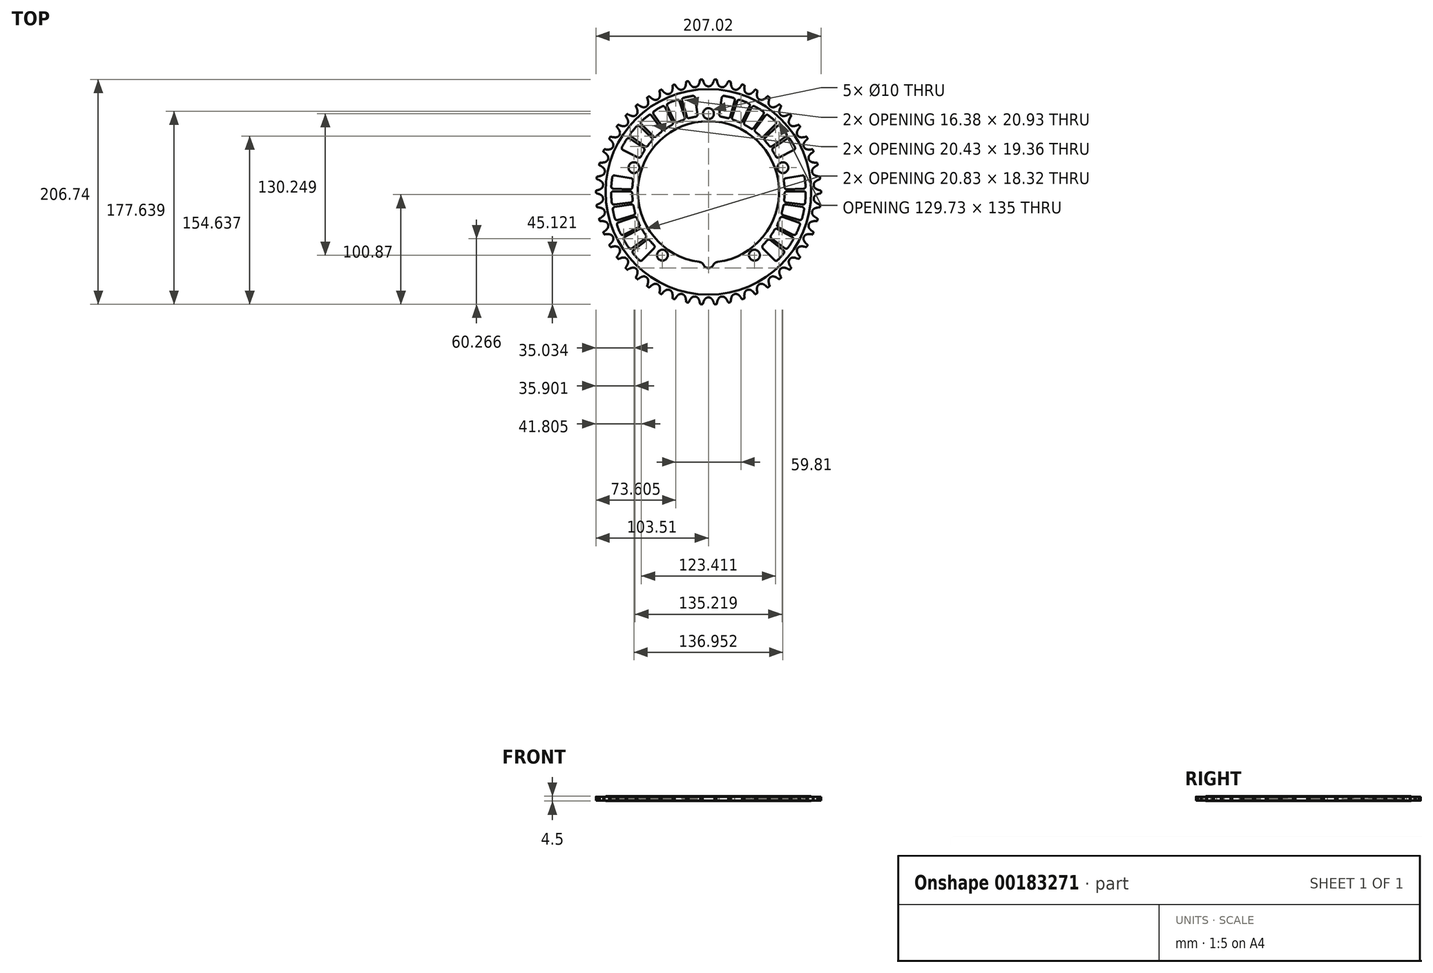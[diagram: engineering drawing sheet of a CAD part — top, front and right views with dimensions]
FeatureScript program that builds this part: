
annotation { "Feature Type Name" : "Feature", "Feature Type Description" : "" }
export const myFeature = defineFeature(function(context is Context, id is Id, definition is map)
    precondition{}
    {
        {
            var Q0;
            Q0=qCreatedBy(makeId("Top.planeOp"),FACE);
            var sketch = newSketch(context, id + "F0", { "sketchPlane" : qUnion([Q0])});
            skCircle(sketch, "E0", {"center": v(0, 0) * mm, "radius": 101.06 * mm, "construction": true});
            skCircle(sketch, "E1", {"center": v(0, 0) * mm, "radius": 65 * mm});
            skCircle(sketch, "E2", {"center": v(0, 72) * mm, "radius": 5 * mm});
            skCircle(sketch, "E3.1.0", {"center": v(-68.48, 22.25) * mm, "radius": 5 * mm});
            skCircle(sketch, "E3.2.0", {"center": v(-42.32, -58.25) * mm, "radius": 5 * mm});
            skCircle(sketch, "E3.3.0", {"center": v(42.32, -58.25) * mm, "radius": 5 * mm});
            skCircle(sketch, "E3.4.0", {"center": v(68.48, 22.25) * mm, "radius": 5 * mm});
            skCircle(sketch, "E4", {"center": v(0, 0) * mm, "radius": 94.55 * mm});
            skArc(sketch, "E5", {"start": v(-3.24, 98.7) * mm, "mid": v(-1.82, 97.48) * mm, "end": v(0, 97.05) * mm});
            skArc(sketch, "E6", {"start": v(-4.68, 101.38) * mm, "mid": v(-4.06, 99.98) * mm, "end": v(-3.24, 98.7) * mm});
            skLineSegment(sketch, "E7", {"start": v(-4.68, 101.38) * mm, "end": v(-5.06, 102.48) * mm});
            skArc(sketch, "E8.trimOffspring", {"start": v(-5.06, 102.48) * mm, "mid": v(-5.7, 103.79) * mm, "end": v(-6.6, 104.92) * mm});
            skArc(sketch, "E9.MirrorCS", {"start": v(3.24, 98.7) * mm, "mid": v(1.82, 97.48) * mm, "end": v(0, 97.05) * mm});
            skArc(sketch, "E10.MirrorCS", {"start": v(4.68, 101.38) * mm, "mid": v(4.06, 99.98) * mm, "end": v(3.24, 98.7) * mm});
            skLineSegment(sketch, "E11.MirrorCS", {"start": v(4.68, 101.38) * mm, "end": v(5.06, 102.48) * mm});
            skArc(sketch, "E12.MirrorCS", {"start": v(5.06, 102.48) * mm, "mid": v(5.7, 103.79) * mm, "end": v(6.6, 104.92) * mm});
            skArc(sketch, "E13.1.0", {"start": v(-17.87, 101.04) * mm, "mid": v(-18.66, 102.26) * mm, "end": v(-19.7, 103.26) * mm});
            skArc(sketch, "E13.1.1", {"start": v(-7.82, 102.31) * mm, "mid": v(-7.36, 103.68) * mm, "end": v(-6.6, 104.92) * mm});
            skLineSegment(sketch, "E13.1.2", {"start": v(-8.07, 101.17) * mm, "end": v(-7.82, 102.31) * mm});
            skArc(sketch, "E13.1.3", {"start": v(-8.07, 101.17) * mm, "mid": v(-8.5, 99.7) * mm, "end": v(-9.15, 98.32) * mm});
            skArc(sketch, "E13.1.4", {"start": v(-9.15, 98.32) * mm, "mid": v(-10.42, 96.94) * mm, "end": v(-12.16, 96.28) * mm});
            skArc(sketch, "E13.1.5", {"start": v(-15.58, 97.5) * mm, "mid": v(-14.02, 96.49) * mm, "end": v(-12.16, 96.28) * mm});
            skArc(sketch, "E13.1.6", {"start": v(-17.35, 100) * mm, "mid": v(-16.56, 98.69) * mm, "end": v(-15.58, 97.5) * mm});
            skLineSegment(sketch, "E13.1.7", {"start": v(-17.35, 100) * mm, "end": v(-17.87, 101.04) * mm});
            skArc(sketch, "E13.2.0", {"start": v(-30.39, 98) * mm, "mid": v(-31.33, 99.11) * mm, "end": v(-32.49, 99.98) * mm});
            skArc(sketch, "E13.2.1", {"start": v(-20.58, 100.52) * mm, "mid": v(-20.3, 101.94) * mm, "end": v(-19.7, 103.26) * mm});
            skLineSegment(sketch, "E13.2.2", {"start": v(-20.68, 99.36) * mm, "end": v(-20.58, 100.52) * mm});
            skArc(sketch, "E13.2.3", {"start": v(-20.68, 99.36) * mm, "mid": v(-20.94, 97.85) * mm, "end": v(-21.4, 96.4) * mm});
            skArc(sketch, "E13.2.4", {"start": v(-21.4, 96.4) * mm, "mid": v(-22.48, 94.87) * mm, "end": v(-24.13, 94) * mm});
            skArc(sketch, "E13.2.5", {"start": v(-27.68, 94.79) * mm, "mid": v(-26, 93.97) * mm, "end": v(-24.13, 94) * mm});
            skArc(sketch, "E13.2.6", {"start": v(-29.74, 97.03) * mm, "mid": v(-28.8, 95.83) * mm, "end": v(-27.68, 94.79) * mm});
            skLineSegment(sketch, "E13.2.7", {"start": v(-29.74, 97.03) * mm, "end": v(-30.39, 98) * mm});
            skArc(sketch, "E13.3.0", {"start": v(-42.43, 93.42) * mm, "mid": v(-43.5, 94.4) * mm, "end": v(-44.76, 95.12) * mm});
            skArc(sketch, "E13.3.1", {"start": v(-33.02, 97.15) * mm, "mid": v(-32.91, 98.6) * mm, "end": v(-32.49, 99.98) * mm});
            skLineSegment(sketch, "E13.3.2", {"start": v(-32.97, 95.98) * mm, "end": v(-33.02, 97.15) * mm});
            skArc(sketch, "E13.3.3", {"start": v(-32.97, 95.98) * mm, "mid": v(-33.03, 94.46) * mm, "end": v(-33.32, 92.95) * mm});
            skArc(sketch, "E13.3.4", {"start": v(-33.32, 92.95) * mm, "mid": v(-34.2, 91.3) * mm, "end": v(-35.73, 90.23) * mm});
            skArc(sketch, "E13.3.5", {"start": v(-39.34, 90.57) * mm, "mid": v(-37.57, 89.97) * mm, "end": v(-35.73, 90.23) * mm});
            skArc(sketch, "E13.3.6", {"start": v(-41.67, 92.54) * mm, "mid": v(-40.58, 91.47) * mm, "end": v(-39.34, 90.57) * mm});
            skLineSegment(sketch, "E13.3.7", {"start": v(-41.67, 92.54) * mm, "end": v(-42.43, 93.42) * mm});
            skArc(sketch, "E13.4.0", {"start": v(-53.8, 87.37) * mm, "mid": v(-54.99, 88.2) * mm, "end": v(-56.33, 88.76) * mm});
            skArc(sketch, "E13.4.1", {"start": v(-44.94, 92.25) * mm, "mid": v(-45.01, 93.7) * mm, "end": v(-44.76, 95.12) * mm});
            skLineSegment(sketch, "E13.4.2", {"start": v(-44.74, 91.1) * mm, "end": v(-44.94, 92.25) * mm});
            skArc(sketch, "E13.4.3", {"start": v(-44.74, 91.1) * mm, "mid": v(-44.61, 89.57) * mm, "end": v(-44.7, 88.05) * mm});
            skArc(sketch, "E13.4.4", {"start": v(-44.7, 88.05) * mm, "mid": v(-45.37, 86.3) * mm, "end": v(-46.75, 85.04) * mm});
            skArc(sketch, "E13.4.5", {"start": v(-50.38, 84.92) * mm, "mid": v(-48.55, 84.55) * mm, "end": v(-46.75, 85.04) * mm});
            skArc(sketch, "E13.4.6", {"start": v(-52.94, 86.59) * mm, "mid": v(-51.72, 85.66) * mm, "end": v(-50.38, 84.92) * mm});
            skLineSegment(sketch, "E13.4.7", {"start": v(-52.94, 86.59) * mm, "end": v(-53.8, 87.37) * mm});
            skArc(sketch, "E13.5.0", {"start": v(-64.33, 79.94) * mm, "mid": v(-65.61, 80.62) * mm, "end": v(-67, 81) * mm});
            skArc(sketch, "E13.5.1", {"start": v(-56.14, 85.89) * mm, "mid": v(-56.4, 87.31) * mm, "end": v(-56.33, 88.76) * mm});
            skLineSegment(sketch, "E13.5.2", {"start": v(-55.8, 84.77) * mm, "end": v(-56.14, 85.89) * mm});
            skArc(sketch, "E13.5.3", {"start": v(-55.8, 84.77) * mm, "mid": v(-55.49, 83.27) * mm, "end": v(-55.39, 81.75) * mm});
            skArc(sketch, "E13.5.4", {"start": v(-55.39, 81.75) * mm, "mid": v(-55.83, 79.93) * mm, "end": v(-57.04, 78.51) * mm});
            skArc(sketch, "E13.5.5", {"start": v(-60.63, 77.94) * mm, "mid": v(-58.77, 77.8) * mm, "end": v(-57.04, 78.51) * mm});
            skArc(sketch, "E13.5.6", {"start": v(-63.37, 79.27) * mm, "mid": v(-62.05, 78.5) * mm, "end": v(-60.63, 77.94) * mm});
            skLineSegment(sketch, "E13.5.7", {"start": v(-63.37, 79.27) * mm, "end": v(-64.33, 79.94) * mm});
            skArc(sketch, "E13.6.0", {"start": v(-73.85, 71.24) * mm, "mid": v(-75.2, 71.76) * mm, "end": v(-76.63, 71.96) * mm});
            skArc(sketch, "E13.6.1", {"start": v(-66.47, 78.17) * mm, "mid": v(-66.9, 79.56) * mm, "end": v(-67, 81) * mm});
            skLineSegment(sketch, "E13.6.2", {"start": v(-66, 77.1) * mm, "end": v(-66.47, 78.17) * mm});
            skArc(sketch, "E13.6.3", {"start": v(-66, 77.1) * mm, "mid": v(-65.49, 75.66) * mm, "end": v(-65.2, 74.16) * mm});
            skArc(sketch, "E13.6.4", {"start": v(-65.2, 74.16) * mm, "mid": v(-65.4, 72.3) * mm, "end": v(-66.43, 70.75) * mm});
            skArc(sketch, "E13.6.5", {"start": v(-69.92, 69.73) * mm, "mid": v(-68.06, 69.82) * mm, "end": v(-66.43, 70.75) * mm});
            skArc(sketch, "E13.6.6", {"start": v(-72.8, 70.7) * mm, "mid": v(-71.4, 70.1) * mm, "end": v(-69.92, 69.73) * mm});
            skLineSegment(sketch, "E13.6.7", {"start": v(-72.8, 70.7) * mm, "end": v(-73.85, 71.24) * mm});
            skArc(sketch, "E13.7.0", {"start": v(-82.2, 61.43) * mm, "mid": v(-83.6, 61.77) * mm, "end": v(-85.05, 61.8) * mm});
            skArc(sketch, "E13.7.1", {"start": v(-75.74, 69.23) * mm, "mid": v(-76.34, 70.54) * mm, "end": v(-76.63, 71.96) * mm});
            skLineSegment(sketch, "E13.7.2", {"start": v(-75.14, 68.23) * mm, "end": v(-75.74, 69.23) * mm});
            skArc(sketch, "E13.7.3", {"start": v(-75.14, 68.23) * mm, "mid": v(-74.45, 66.86) * mm, "end": v(-73.98, 65.4) * mm});
            skArc(sketch, "E13.7.4", {"start": v(-73.98, 65.4) * mm, "mid": v(-73.95, 63.54) * mm, "end": v(-74.78, 61.86) * mm});
            skArc(sketch, "E13.7.5", {"start": v(-78.1, 60.41) * mm, "mid": v(-76.27, 60.74) * mm, "end": v(-74.78, 61.86) * mm});
            skArc(sketch, "E13.7.6", {"start": v(-81.1, 61.02) * mm, "mid": v(-79.62, 60.6) * mm, "end": v(-78.1, 60.41) * mm});
            skLineSegment(sketch, "E13.7.7", {"start": v(-81.1, 61.02) * mm, "end": v(-82.2, 61.43) * mm});
            skArc(sketch, "E13.8.0", {"start": v(-89.24, 50.64) * mm, "mid": v(-90.68, 50.8) * mm, "end": v(-92.12, 50.64) * mm});
            skArc(sketch, "E13.8.1", {"start": v(-83.82, 59.19) * mm, "mid": v(-84.58, 60.42) * mm, "end": v(-85.05, 61.8) * mm});
            skLineSegment(sketch, "E13.8.2", {"start": v(-83.1, 58.27) * mm, "end": v(-83.82, 59.19) * mm});
            skArc(sketch, "E13.8.3", {"start": v(-83.1, 58.27) * mm, "mid": v(-82.25, 57) * mm, "end": v(-81.6, 55.62) * mm});
            skArc(sketch, "E13.8.4", {"start": v(-81.6, 55.62) * mm, "mid": v(-81.33, 53.77) * mm, "end": v(-81.94, 52) * mm});
            skArc(sketch, "E13.8.5", {"start": v(-85.06, 50.15) * mm, "mid": v(-83.28, 50.7) * mm, "end": v(-81.94, 52) * mm});
            skArc(sketch, "E13.8.6", {"start": v(-88.1, 50.38) * mm, "mid": v(-86.6, 50.15) * mm, "end": v(-85.06, 50.15) * mm});
            skLineSegment(sketch, "E13.8.7", {"start": v(-88.1, 50.38) * mm, "end": v(-89.24, 50.64) * mm});
            skArc(sketch, "E13.9.0", {"start": v(-94.89, 39.06) * mm, "mid": v(-96.33, 39.04) * mm, "end": v(-97.74, 38.7) * mm});
            skArc(sketch, "E13.9.1", {"start": v(-90.58, 48.22) * mm, "mid": v(-91.49, 49.34) * mm, "end": v(-92.12, 50.64) * mm});
            skLineSegment(sketch, "E13.9.2", {"start": v(-89.74, 47.4) * mm, "end": v(-90.58, 48.22) * mm});
            skArc(sketch, "E13.9.3", {"start": v(-89.74, 47.4) * mm, "mid": v(-88.74, 46.24) * mm, "end": v(-87.92, 44.95) * mm});
            skArc(sketch, "E13.9.4", {"start": v(-87.92, 44.95) * mm, "mid": v(-87.43, 43.15) * mm, "end": v(-87.81, 41.32) * mm});
            skArc(sketch, "E13.9.5", {"start": v(-90.68, 39.09) * mm, "mid": v(-88.98, 39.86) * mm, "end": v(-87.81, 41.32) * mm});
            skArc(sketch, "E13.9.6", {"start": v(-93.72, 38.94) * mm, "mid": v(-92.2, 38.9) * mm, "end": v(-90.68, 39.09) * mm});
            skLineSegment(sketch, "E13.9.7", {"start": v(-93.72, 38.94) * mm, "end": v(-94.89, 39.06) * mm});
            skArc(sketch, "E13.10.0", {"start": v(-99.03, 26.85) * mm, "mid": v(-100.47, 26.66) * mm, "end": v(-101.82, 26.14) * mm});
            skArc(sketch, "E13.10.1", {"start": v(-95.9, 36.48) * mm, "mid": v(-96.95, 37.49) * mm, "end": v(-97.74, 38.7) * mm});
            skLineSegment(sketch, "E13.10.2", {"start": v(-94.97, 35.78) * mm, "end": v(-95.9, 36.48) * mm});
            skArc(sketch, "E13.10.3", {"start": v(-94.97, 35.78) * mm, "mid": v(-93.84, 34.76) * mm, "end": v(-92.86, 33.58) * mm});
            skArc(sketch, "E13.10.4", {"start": v(-92.86, 33.58) * mm, "mid": v(-92.15, 31.85) * mm, "end": v(-92.3, 29.99) * mm});
            skArc(sketch, "E13.10.5", {"start": v(-94.86, 27.42) * mm, "mid": v(-93.27, 28.4) * mm, "end": v(-92.3, 29.99) * mm});
            skArc(sketch, "E13.10.6", {"start": v(-97.86, 26.88) * mm, "mid": v(-96.34, 27.04) * mm, "end": v(-94.86, 27.42) * mm});
            skLineSegment(sketch, "E13.10.7", {"start": v(-97.86, 26.88) * mm, "end": v(-99.03, 26.85) * mm});
            skArc(sketch, "E13.11.0", {"start": v(-101.62, 14.23) * mm, "mid": v(-103.02, 13.86) * mm, "end": v(-104.3, 13.18) * mm});
            skArc(sketch, "E13.11.1", {"start": v(-99.72, 24.18) * mm, "mid": v(-100.88, 25.04) * mm, "end": v(-101.82, 26.14) * mm});
            skLineSegment(sketch, "E13.11.2", {"start": v(-98.7, 23.59) * mm, "end": v(-99.72, 24.18) * mm});
            skArc(sketch, "E13.11.3", {"start": v(-98.7, 23.59) * mm, "mid": v(-97.45, 22.72) * mm, "end": v(-96.34, 21.68) * mm});
            skArc(sketch, "E13.11.4", {"start": v(-96.34, 21.68) * mm, "mid": v(-95.42, 20.05) * mm, "end": v(-95.33, 18.19) * mm});
            skArc(sketch, "E13.11.5", {"start": v(-97.55, 15.31) * mm, "mid": v(-96.1, 16.48) * mm, "end": v(-95.33, 18.19) * mm});
            skArc(sketch, "E13.11.6", {"start": v(-100.46, 14.4) * mm, "mid": v(-98.97, 14.75) * mm, "end": v(-97.55, 15.31) * mm});
            skLineSegment(sketch, "E13.11.7", {"start": v(-100.46, 14.4) * mm, "end": v(-101.62, 14.23) * mm});
            skArc(sketch, "E13.12.0", {"start": v(-102.6, 1.38) * mm, "mid": v(-103.94, 0.84) * mm, "end": v(-105.13, 0) * mm});
            skArc(sketch, "E13.12.1", {"start": v(-101.96, 11.49) * mm, "mid": v(-103.23, 12.2) * mm, "end": v(-104.3, 13.18) * mm});
            skLineSegment(sketch, "E13.12.2", {"start": v(-100.89, 11.03) * mm, "end": v(-101.96, 11.49) * mm});
            skArc(sketch, "E13.12.3", {"start": v(-100.89, 11.03) * mm, "mid": v(-99.53, 10.33) * mm, "end": v(-98.3, 9.43) * mm});
            skArc(sketch, "E13.12.4", {"start": v(-98.3, 9.43) * mm, "mid": v(-97.18, 7.93) * mm, "end": v(-96.86, 6.1) * mm});
            skArc(sketch, "E13.12.5", {"start": v(-98.7, 2.96) * mm, "mid": v(-97.4, 4.3) * mm, "end": v(-96.86, 6.1) * mm});
            skArc(sketch, "E13.12.6", {"start": v(-101.47, 1.7) * mm, "mid": v(-100.04, 2.23) * mm, "end": v(-98.7, 2.96) * mm});
            skLineSegment(sketch, "E13.12.7", {"start": v(-101.47, 1.7) * mm, "end": v(-102.6, 1.38) * mm});
            skArc(sketch, "E13.13.0", {"start": v(-101.96, -11.49) * mm, "mid": v(-103.23, -12.2) * mm, "end": v(-104.3, -13.18) * mm});
            skArc(sketch, "E13.13.1", {"start": v(-102.6, -1.38) * mm, "mid": v(-103.94, -0.84) * mm, "end": v(-105.13, 0) * mm});
            skLineSegment(sketch, "E13.13.2", {"start": v(-101.47, -1.7) * mm, "end": v(-102.6, -1.38) * mm});
            skArc(sketch, "E13.13.3", {"start": v(-101.47, -1.7) * mm, "mid": v(-100.04, -2.23) * mm, "end": v(-98.7, -2.96) * mm});
            skArc(sketch, "E13.13.4", {"start": v(-98.7, -2.96) * mm, "mid": v(-97.4, -4.3) * mm, "end": v(-96.86, -6.1) * mm});
            skArc(sketch, "E13.13.5", {"start": v(-98.3, -9.43) * mm, "mid": v(-97.18, -7.93) * mm, "end": v(-96.86, -6.1) * mm});
            skArc(sketch, "E13.13.6", {"start": v(-100.89, -11.03) * mm, "mid": v(-99.53, -10.33) * mm, "end": v(-98.3, -9.43) * mm});
            skLineSegment(sketch, "E13.13.7", {"start": v(-100.89, -11.03) * mm, "end": v(-101.96, -11.49) * mm});
            skArc(sketch, "E13.14.0", {"start": v(-99.72, -24.18) * mm, "mid": v(-100.88, -25.04) * mm, "end": v(-101.82, -26.14) * mm});
            skArc(sketch, "E13.14.1", {"start": v(-101.62, -14.23) * mm, "mid": v(-103.02, -13.86) * mm, "end": v(-104.3, -13.18) * mm});
            skLineSegment(sketch, "E13.14.2", {"start": v(-100.46, -14.4) * mm, "end": v(-101.62, -14.23) * mm});
            skArc(sketch, "E13.14.3", {"start": v(-100.46, -14.4) * mm, "mid": v(-98.97, -14.75) * mm, "end": v(-97.55, -15.31) * mm});
            skArc(sketch, "E13.14.4", {"start": v(-97.55, -15.31) * mm, "mid": v(-96.1, -16.48) * mm, "end": v(-95.33, -18.19) * mm});
            skArc(sketch, "E13.14.5", {"start": v(-96.34, -21.68) * mm, "mid": v(-95.42, -20.05) * mm, "end": v(-95.33, -18.19) * mm});
            skArc(sketch, "E13.14.6", {"start": v(-98.7, -23.59) * mm, "mid": v(-97.45, -22.72) * mm, "end": v(-96.34, -21.68) * mm});
            skLineSegment(sketch, "E13.14.7", {"start": v(-98.7, -23.59) * mm, "end": v(-99.72, -24.18) * mm});
            skArc(sketch, "E13.15.0", {"start": v(-95.9, -36.48) * mm, "mid": v(-96.95, -37.49) * mm, "end": v(-97.74, -38.7) * mm});
            skArc(sketch, "E13.15.1", {"start": v(-99.03, -26.85) * mm, "mid": v(-100.47, -26.66) * mm, "end": v(-101.82, -26.14) * mm});
            skLineSegment(sketch, "E13.15.2", {"start": v(-97.86, -26.88) * mm, "end": v(-99.03, -26.85) * mm});
            skArc(sketch, "E13.15.3", {"start": v(-97.86, -26.88) * mm, "mid": v(-96.34, -27.04) * mm, "end": v(-94.86, -27.42) * mm});
            skArc(sketch, "E13.15.4", {"start": v(-94.86, -27.42) * mm, "mid": v(-93.27, -28.4) * mm, "end": v(-92.3, -29.99) * mm});
            skArc(sketch, "E13.15.5", {"start": v(-92.86, -33.58) * mm, "mid": v(-92.15, -31.85) * mm, "end": v(-92.3, -29.99) * mm});
            skArc(sketch, "E13.15.6", {"start": v(-94.97, -35.78) * mm, "mid": v(-93.84, -34.76) * mm, "end": v(-92.86, -33.58) * mm});
            skLineSegment(sketch, "E13.15.7", {"start": v(-94.97, -35.78) * mm, "end": v(-95.9, -36.48) * mm});
            skArc(sketch, "E13.16.0", {"start": v(-90.58, -48.22) * mm, "mid": v(-91.49, -49.34) * mm, "end": v(-92.12, -50.64) * mm});
            skArc(sketch, "E13.16.1", {"start": v(-94.89, -39.06) * mm, "mid": v(-96.33, -39.04) * mm, "end": v(-97.74, -38.7) * mm});
            skLineSegment(sketch, "E13.16.2", {"start": v(-93.72, -38.94) * mm, "end": v(-94.89, -39.06) * mm});
            skArc(sketch, "E13.16.3", {"start": v(-93.72, -38.94) * mm, "mid": v(-92.2, -38.9) * mm, "end": v(-90.68, -39.09) * mm});
            skArc(sketch, "E13.16.4", {"start": v(-90.68, -39.09) * mm, "mid": v(-88.98, -39.86) * mm, "end": v(-87.81, -41.32) * mm});
            skArc(sketch, "E13.16.5", {"start": v(-87.92, -44.95) * mm, "mid": v(-87.43, -43.15) * mm, "end": v(-87.81, -41.32) * mm});
            skArc(sketch, "E13.16.6", {"start": v(-89.74, -47.4) * mm, "mid": v(-88.74, -46.24) * mm, "end": v(-87.92, -44.95) * mm});
            skLineSegment(sketch, "E13.16.7", {"start": v(-89.74, -47.4) * mm, "end": v(-90.58, -48.22) * mm});
            skArc(sketch, "E13.17.0", {"start": v(-83.82, -59.19) * mm, "mid": v(-84.58, -60.42) * mm, "end": v(-85.05, -61.8) * mm});
            skArc(sketch, "E13.17.1", {"start": v(-89.24, -50.64) * mm, "mid": v(-90.68, -50.8) * mm, "end": v(-92.12, -50.64) * mm});
            skLineSegment(sketch, "E13.17.2", {"start": v(-88.1, -50.38) * mm, "end": v(-89.24, -50.64) * mm});
            skArc(sketch, "E13.17.3", {"start": v(-88.1, -50.38) * mm, "mid": v(-86.6, -50.15) * mm, "end": v(-85.06, -50.15) * mm});
            skArc(sketch, "E13.17.4", {"start": v(-85.06, -50.15) * mm, "mid": v(-83.28, -50.7) * mm, "end": v(-81.94, -52) * mm});
            skArc(sketch, "E13.17.5", {"start": v(-81.6, -55.62) * mm, "mid": v(-81.33, -53.77) * mm, "end": v(-81.94, -52) * mm});
            skArc(sketch, "E13.17.6", {"start": v(-83.1, -58.27) * mm, "mid": v(-82.25, -57) * mm, "end": v(-81.6, -55.62) * mm});
            skLineSegment(sketch, "E13.17.7", {"start": v(-83.1, -58.27) * mm, "end": v(-83.82, -59.19) * mm});
            skArc(sketch, "E13.18.0", {"start": v(-75.74, -69.23) * mm, "mid": v(-76.34, -70.54) * mm, "end": v(-76.63, -71.96) * mm});
            skArc(sketch, "E13.18.1", {"start": v(-82.2, -61.43) * mm, "mid": v(-83.6, -61.77) * mm, "end": v(-85.05, -61.8) * mm});
            skLineSegment(sketch, "E13.18.2", {"start": v(-81.1, -61.02) * mm, "end": v(-82.2, -61.43) * mm});
            skArc(sketch, "E13.18.3", {"start": v(-81.1, -61.02) * mm, "mid": v(-79.62, -60.6) * mm, "end": v(-78.1, -60.41) * mm});
            skArc(sketch, "E13.18.4", {"start": v(-78.1, -60.41) * mm, "mid": v(-76.27, -60.74) * mm, "end": v(-74.78, -61.86) * mm});
            skArc(sketch, "E13.18.5", {"start": v(-73.98, -65.4) * mm, "mid": v(-73.95, -63.54) * mm, "end": v(-74.78, -61.86) * mm});
            skArc(sketch, "E13.18.6", {"start": v(-75.14, -68.23) * mm, "mid": v(-74.45, -66.86) * mm, "end": v(-73.98, -65.4) * mm});
            skLineSegment(sketch, "E13.18.7", {"start": v(-75.14, -68.23) * mm, "end": v(-75.74, -69.23) * mm});
            skArc(sketch, "E13.19.0", {"start": v(-66.47, -78.17) * mm, "mid": v(-66.9, -79.56) * mm, "end": v(-67, -81) * mm});
            skArc(sketch, "E13.19.1", {"start": v(-73.85, -71.24) * mm, "mid": v(-75.2, -71.76) * mm, "end": v(-76.63, -71.96) * mm});
            skLineSegment(sketch, "E13.19.2", {"start": v(-72.8, -70.7) * mm, "end": v(-73.85, -71.24) * mm});
            skArc(sketch, "E13.19.3", {"start": v(-72.8, -70.7) * mm, "mid": v(-71.4, -70.1) * mm, "end": v(-69.92, -69.73) * mm});
            skArc(sketch, "E13.19.4", {"start": v(-69.92, -69.73) * mm, "mid": v(-68.06, -69.82) * mm, "end": v(-66.43, -70.75) * mm});
            skArc(sketch, "E13.19.5", {"start": v(-65.2, -74.16) * mm, "mid": v(-65.4, -72.3) * mm, "end": v(-66.43, -70.75) * mm});
            skArc(sketch, "E13.19.6", {"start": v(-66, -77.1) * mm, "mid": v(-65.49, -75.66) * mm, "end": v(-65.2, -74.16) * mm});
            skLineSegment(sketch, "E13.19.7", {"start": v(-66, -77.1) * mm, "end": v(-66.47, -78.17) * mm});
            skArc(sketch, "E13.20.0", {"start": v(-56.14, -85.89) * mm, "mid": v(-56.4, -87.31) * mm, "end": v(-56.33, -88.76) * mm});
            skArc(sketch, "E13.20.1", {"start": v(-64.33, -79.94) * mm, "mid": v(-65.61, -80.62) * mm, "end": v(-67, -81) * mm});
            skLineSegment(sketch, "E13.20.2", {"start": v(-63.37, -79.27) * mm, "end": v(-64.33, -79.94) * mm});
            skArc(sketch, "E13.20.3", {"start": v(-63.37, -79.27) * mm, "mid": v(-62.05, -78.5) * mm, "end": v(-60.63, -77.94) * mm});
            skArc(sketch, "E13.20.4", {"start": v(-60.63, -77.94) * mm, "mid": v(-58.77, -77.8) * mm, "end": v(-57.04, -78.51) * mm});
            skArc(sketch, "E13.20.5", {"start": v(-55.39, -81.75) * mm, "mid": v(-55.83, -79.93) * mm, "end": v(-57.04, -78.51) * mm});
            skArc(sketch, "E13.20.6", {"start": v(-55.8, -84.77) * mm, "mid": v(-55.49, -83.27) * mm, "end": v(-55.39, -81.75) * mm});
            skLineSegment(sketch, "E13.20.7", {"start": v(-55.8, -84.77) * mm, "end": v(-56.14, -85.89) * mm});
            skArc(sketch, "E13.21.0", {"start": v(-44.94, -92.25) * mm, "mid": v(-45.01, -93.7) * mm, "end": v(-44.76, -95.12) * mm});
            skArc(sketch, "E13.21.1", {"start": v(-53.8, -87.37) * mm, "mid": v(-54.99, -88.2) * mm, "end": v(-56.33, -88.76) * mm});
            skLineSegment(sketch, "E13.21.2", {"start": v(-52.94, -86.59) * mm, "end": v(-53.8, -87.37) * mm});
            skArc(sketch, "E13.21.3", {"start": v(-52.94, -86.59) * mm, "mid": v(-51.72, -85.66) * mm, "end": v(-50.38, -84.92) * mm});
            skArc(sketch, "E13.21.4", {"start": v(-50.38, -84.92) * mm, "mid": v(-48.55, -84.55) * mm, "end": v(-46.75, -85.04) * mm});
            skArc(sketch, "E13.21.5", {"start": v(-44.7, -88.05) * mm, "mid": v(-45.37, -86.3) * mm, "end": v(-46.75, -85.04) * mm});
            skArc(sketch, "E13.21.6", {"start": v(-44.74, -91.1) * mm, "mid": v(-44.61, -89.57) * mm, "end": v(-44.7, -88.05) * mm});
            skLineSegment(sketch, "E13.21.7", {"start": v(-44.74, -91.1) * mm, "end": v(-44.94, -92.25) * mm});
            skArc(sketch, "E13.22.0", {"start": v(-33.02, -97.15) * mm, "mid": v(-32.91, -98.6) * mm, "end": v(-32.49, -99.98) * mm});
            skArc(sketch, "E13.22.1", {"start": v(-42.43, -93.42) * mm, "mid": v(-43.5, -94.4) * mm, "end": v(-44.76, -95.12) * mm});
            skLineSegment(sketch, "E13.22.2", {"start": v(-41.67, -92.54) * mm, "end": v(-42.43, -93.42) * mm});
            skArc(sketch, "E13.22.3", {"start": v(-41.67, -92.54) * mm, "mid": v(-40.58, -91.47) * mm, "end": v(-39.34, -90.57) * mm});
            skArc(sketch, "E13.22.4", {"start": v(-39.34, -90.57) * mm, "mid": v(-37.57, -89.97) * mm, "end": v(-35.73, -90.23) * mm});
            skArc(sketch, "E13.22.5", {"start": v(-33.32, -92.95) * mm, "mid": v(-34.2, -91.3) * mm, "end": v(-35.73, -90.23) * mm});
            skArc(sketch, "E13.22.6", {"start": v(-32.97, -95.98) * mm, "mid": v(-33.03, -94.46) * mm, "end": v(-33.32, -92.95) * mm});
            skLineSegment(sketch, "E13.22.7", {"start": v(-32.97, -95.98) * mm, "end": v(-33.02, -97.15) * mm});
            skArc(sketch, "E13.23.0", {"start": v(-20.58, -100.52) * mm, "mid": v(-20.3, -101.94) * mm, "end": v(-19.7, -103.26) * mm});
            skArc(sketch, "E13.23.1", {"start": v(-30.39, -98) * mm, "mid": v(-31.33, -99.11) * mm, "end": v(-32.49, -99.98) * mm});
            skLineSegment(sketch, "E13.23.2", {"start": v(-29.74, -97.03) * mm, "end": v(-30.39, -98) * mm});
            skArc(sketch, "E13.23.3", {"start": v(-29.74, -97.03) * mm, "mid": v(-28.8, -95.83) * mm, "end": v(-27.68, -94.79) * mm});
            skArc(sketch, "E13.23.4", {"start": v(-27.68, -94.79) * mm, "mid": v(-26, -93.97) * mm, "end": v(-24.13, -94) * mm});
            skArc(sketch, "E13.23.5", {"start": v(-21.4, -96.4) * mm, "mid": v(-22.48, -94.87) * mm, "end": v(-24.13, -94) * mm});
            skArc(sketch, "E13.23.6", {"start": v(-20.68, -99.36) * mm, "mid": v(-20.94, -97.85) * mm, "end": v(-21.4, -96.4) * mm});
            skLineSegment(sketch, "E13.23.7", {"start": v(-20.68, -99.36) * mm, "end": v(-20.58, -100.52) * mm});
            skArc(sketch, "E13.24.0", {"start": v(-7.82, -102.31) * mm, "mid": v(-7.36, -103.68) * mm, "end": v(-6.6, -104.92) * mm});
            skArc(sketch, "E13.24.1", {"start": v(-17.87, -101.04) * mm, "mid": v(-18.66, -102.26) * mm, "end": v(-19.7, -103.26) * mm});
            skLineSegment(sketch, "E13.24.2", {"start": v(-17.35, -100) * mm, "end": v(-17.87, -101.04) * mm});
            skArc(sketch, "E13.24.3", {"start": v(-17.35, -100) * mm, "mid": v(-16.56, -98.69) * mm, "end": v(-15.58, -97.5) * mm});
            skArc(sketch, "E13.24.4", {"start": v(-15.58, -97.5) * mm, "mid": v(-14.02, -96.49) * mm, "end": v(-12.16, -96.28) * mm});
            skArc(sketch, "E13.24.5", {"start": v(-9.15, -98.32) * mm, "mid": v(-10.42, -96.94) * mm, "end": v(-12.16, -96.28) * mm});
            skArc(sketch, "E13.24.6", {"start": v(-8.07, -101.17) * mm, "mid": v(-8.5, -99.7) * mm, "end": v(-9.15, -98.32) * mm});
            skLineSegment(sketch, "E13.24.7", {"start": v(-8.07, -101.17) * mm, "end": v(-7.82, -102.31) * mm});
            skArc(sketch, "E13.25.0", {"start": v(5.06, -102.48) * mm, "mid": v(5.7, -103.79) * mm, "end": v(6.6, -104.92) * mm});
            skArc(sketch, "E13.25.1", {"start": v(-5.06, -102.48) * mm, "mid": v(-5.7, -103.79) * mm, "end": v(-6.6, -104.92) * mm});
            skLineSegment(sketch, "E13.25.2", {"start": v(-4.68, -101.38) * mm, "end": v(-5.06, -102.48) * mm});
            skArc(sketch, "E13.25.3", {"start": v(-4.68, -101.38) * mm, "mid": v(-4.06, -99.98) * mm, "end": v(-3.24, -98.7) * mm});
            skArc(sketch, "E13.25.4", {"start": v(-3.24, -98.7) * mm, "mid": v(-1.82, -97.48) * mm, "end": v(0, -97.05) * mm});
            skArc(sketch, "E13.25.5", {"start": v(3.24, -98.7) * mm, "mid": v(1.82, -97.48) * mm, "end": v(0, -97.05) * mm});
            skArc(sketch, "E13.25.6", {"start": v(4.68, -101.38) * mm, "mid": v(4.06, -99.98) * mm, "end": v(3.24, -98.7) * mm});
            skLineSegment(sketch, "E13.25.7", {"start": v(4.68, -101.38) * mm, "end": v(5.06, -102.48) * mm});
            skArc(sketch, "E13.26.0", {"start": v(17.87, -101.04) * mm, "mid": v(18.66, -102.26) * mm, "end": v(19.7, -103.26) * mm});
            skArc(sketch, "E13.26.1", {"start": v(7.82, -102.31) * mm, "mid": v(7.36, -103.68) * mm, "end": v(6.6, -104.92) * mm});
            skLineSegment(sketch, "E13.26.2", {"start": v(8.07, -101.17) * mm, "end": v(7.82, -102.31) * mm});
            skArc(sketch, "E13.26.3", {"start": v(8.07, -101.17) * mm, "mid": v(8.5, -99.7) * mm, "end": v(9.15, -98.32) * mm});
            skArc(sketch, "E13.26.4", {"start": v(9.15, -98.32) * mm, "mid": v(10.42, -96.94) * mm, "end": v(12.16, -96.28) * mm});
            skArc(sketch, "E13.26.5", {"start": v(15.58, -97.5) * mm, "mid": v(14.02, -96.49) * mm, "end": v(12.16, -96.28) * mm});
            skArc(sketch, "E13.26.6", {"start": v(17.35, -100) * mm, "mid": v(16.56, -98.69) * mm, "end": v(15.58, -97.5) * mm});
            skLineSegment(sketch, "E13.26.7", {"start": v(17.35, -100) * mm, "end": v(17.87, -101.04) * mm});
            skArc(sketch, "E13.27.0", {"start": v(30.39, -98) * mm, "mid": v(31.33, -99.11) * mm, "end": v(32.49, -99.98) * mm});
            skArc(sketch, "E13.27.1", {"start": v(20.58, -100.52) * mm, "mid": v(20.3, -101.94) * mm, "end": v(19.7, -103.26) * mm});
            skLineSegment(sketch, "E13.27.2", {"start": v(20.68, -99.36) * mm, "end": v(20.58, -100.52) * mm});
            skArc(sketch, "E13.27.3", {"start": v(20.68, -99.36) * mm, "mid": v(20.94, -97.85) * mm, "end": v(21.4, -96.4) * mm});
            skArc(sketch, "E13.27.4", {"start": v(21.4, -96.4) * mm, "mid": v(22.48, -94.87) * mm, "end": v(24.13, -94) * mm});
            skArc(sketch, "E13.27.5", {"start": v(27.68, -94.79) * mm, "mid": v(26, -93.97) * mm, "end": v(24.13, -94) * mm});
            skArc(sketch, "E13.27.6", {"start": v(29.74, -97.03) * mm, "mid": v(28.8, -95.83) * mm, "end": v(27.68, -94.79) * mm});
            skLineSegment(sketch, "E13.27.7", {"start": v(29.74, -97.03) * mm, "end": v(30.39, -98) * mm});
            skArc(sketch, "E13.28.0", {"start": v(42.43, -93.42) * mm, "mid": v(43.5, -94.4) * mm, "end": v(44.76, -95.12) * mm});
            skArc(sketch, "E13.28.1", {"start": v(33.02, -97.15) * mm, "mid": v(32.91, -98.6) * mm, "end": v(32.49, -99.98) * mm});
            skLineSegment(sketch, "E13.28.2", {"start": v(32.97, -95.98) * mm, "end": v(33.02, -97.15) * mm});
            skArc(sketch, "E13.28.3", {"start": v(32.97, -95.98) * mm, "mid": v(33.03, -94.46) * mm, "end": v(33.32, -92.95) * mm});
            skArc(sketch, "E13.28.4", {"start": v(33.32, -92.95) * mm, "mid": v(34.2, -91.3) * mm, "end": v(35.73, -90.23) * mm});
            skArc(sketch, "E13.28.5", {"start": v(39.34, -90.57) * mm, "mid": v(37.57, -89.97) * mm, "end": v(35.73, -90.23) * mm});
            skArc(sketch, "E13.28.6", {"start": v(41.67, -92.54) * mm, "mid": v(40.58, -91.47) * mm, "end": v(39.34, -90.57) * mm});
            skLineSegment(sketch, "E13.28.7", {"start": v(41.67, -92.54) * mm, "end": v(42.43, -93.42) * mm});
            skArc(sketch, "E13.29.0", {"start": v(53.8, -87.37) * mm, "mid": v(54.99, -88.2) * mm, "end": v(56.33, -88.76) * mm});
            skArc(sketch, "E13.29.1", {"start": v(44.94, -92.25) * mm, "mid": v(45.01, -93.7) * mm, "end": v(44.76, -95.12) * mm});
            skLineSegment(sketch, "E13.29.2", {"start": v(44.74, -91.1) * mm, "end": v(44.94, -92.25) * mm});
            skArc(sketch, "E13.29.3", {"start": v(44.74, -91.1) * mm, "mid": v(44.61, -89.57) * mm, "end": v(44.7, -88.05) * mm});
            skArc(sketch, "E13.29.4", {"start": v(44.7, -88.05) * mm, "mid": v(45.37, -86.3) * mm, "end": v(46.75, -85.04) * mm});
            skArc(sketch, "E13.29.5", {"start": v(50.38, -84.92) * mm, "mid": v(48.55, -84.55) * mm, "end": v(46.75, -85.04) * mm});
            skArc(sketch, "E13.29.6", {"start": v(52.94, -86.59) * mm, "mid": v(51.72, -85.66) * mm, "end": v(50.38, -84.92) * mm});
            skLineSegment(sketch, "E13.29.7", {"start": v(52.94, -86.59) * mm, "end": v(53.8, -87.37) * mm});
            skArc(sketch, "E13.30.0", {"start": v(64.33, -79.94) * mm, "mid": v(65.61, -80.62) * mm, "end": v(67, -81) * mm});
            skArc(sketch, "E13.30.1", {"start": v(56.14, -85.89) * mm, "mid": v(56.4, -87.31) * mm, "end": v(56.33, -88.76) * mm});
            skLineSegment(sketch, "E13.30.2", {"start": v(55.8, -84.77) * mm, "end": v(56.14, -85.89) * mm});
            skArc(sketch, "E13.30.3", {"start": v(55.8, -84.77) * mm, "mid": v(55.49, -83.27) * mm, "end": v(55.39, -81.75) * mm});
            skArc(sketch, "E13.30.4", {"start": v(55.39, -81.75) * mm, "mid": v(55.83, -79.93) * mm, "end": v(57.04, -78.51) * mm});
            skArc(sketch, "E13.30.5", {"start": v(60.63, -77.94) * mm, "mid": v(58.77, -77.8) * mm, "end": v(57.04, -78.51) * mm});
            skArc(sketch, "E13.30.6", {"start": v(63.37, -79.27) * mm, "mid": v(62.05, -78.5) * mm, "end": v(60.63, -77.94) * mm});
            skLineSegment(sketch, "E13.30.7", {"start": v(63.37, -79.27) * mm, "end": v(64.33, -79.94) * mm});
            skArc(sketch, "E13.31.0", {"start": v(73.85, -71.24) * mm, "mid": v(75.2, -71.76) * mm, "end": v(76.63, -71.96) * mm});
            skArc(sketch, "E13.31.1", {"start": v(66.47, -78.17) * mm, "mid": v(66.9, -79.56) * mm, "end": v(67, -81) * mm});
            skLineSegment(sketch, "E13.31.2", {"start": v(66, -77.1) * mm, "end": v(66.47, -78.17) * mm});
            skArc(sketch, "E13.31.3", {"start": v(66, -77.1) * mm, "mid": v(65.49, -75.66) * mm, "end": v(65.2, -74.16) * mm});
            skArc(sketch, "E13.31.4", {"start": v(65.2, -74.16) * mm, "mid": v(65.4, -72.3) * mm, "end": v(66.43, -70.75) * mm});
            skArc(sketch, "E13.31.5", {"start": v(69.92, -69.73) * mm, "mid": v(68.06, -69.82) * mm, "end": v(66.43, -70.75) * mm});
            skArc(sketch, "E13.31.6", {"start": v(72.8, -70.7) * mm, "mid": v(71.4, -70.1) * mm, "end": v(69.92, -69.73) * mm});
            skLineSegment(sketch, "E13.31.7", {"start": v(72.8, -70.7) * mm, "end": v(73.85, -71.24) * mm});
            skArc(sketch, "E13.32.0", {"start": v(82.2, -61.43) * mm, "mid": v(83.6, -61.77) * mm, "end": v(85.05, -61.8) * mm});
            skArc(sketch, "E13.32.1", {"start": v(75.74, -69.23) * mm, "mid": v(76.34, -70.54) * mm, "end": v(76.63, -71.96) * mm});
            skLineSegment(sketch, "E13.32.2", {"start": v(75.14, -68.23) * mm, "end": v(75.74, -69.23) * mm});
            skArc(sketch, "E13.32.3", {"start": v(75.14, -68.23) * mm, "mid": v(74.45, -66.86) * mm, "end": v(73.98, -65.4) * mm});
            skArc(sketch, "E13.32.4", {"start": v(73.98, -65.4) * mm, "mid": v(73.95, -63.54) * mm, "end": v(74.78, -61.86) * mm});
            skArc(sketch, "E13.32.5", {"start": v(78.1, -60.41) * mm, "mid": v(76.27, -60.74) * mm, "end": v(74.78, -61.86) * mm});
            skArc(sketch, "E13.32.6", {"start": v(81.1, -61.02) * mm, "mid": v(79.62, -60.6) * mm, "end": v(78.1, -60.41) * mm});
            skLineSegment(sketch, "E13.32.7", {"start": v(81.1, -61.02) * mm, "end": v(82.2, -61.43) * mm});
            skArc(sketch, "E13.33.0", {"start": v(89.24, -50.64) * mm, "mid": v(90.68, -50.8) * mm, "end": v(92.12, -50.64) * mm});
            skArc(sketch, "E13.33.1", {"start": v(83.82, -59.19) * mm, "mid": v(84.58, -60.42) * mm, "end": v(85.05, -61.8) * mm});
            skLineSegment(sketch, "E13.33.2", {"start": v(83.1, -58.27) * mm, "end": v(83.82, -59.19) * mm});
            skArc(sketch, "E13.33.3", {"start": v(83.1, -58.27) * mm, "mid": v(82.25, -57) * mm, "end": v(81.6, -55.62) * mm});
            skArc(sketch, "E13.33.4", {"start": v(81.6, -55.62) * mm, "mid": v(81.33, -53.77) * mm, "end": v(81.94, -52) * mm});
            skArc(sketch, "E13.33.5", {"start": v(85.06, -50.15) * mm, "mid": v(83.28, -50.7) * mm, "end": v(81.94, -52) * mm});
            skArc(sketch, "E13.33.6", {"start": v(88.1, -50.38) * mm, "mid": v(86.6, -50.15) * mm, "end": v(85.06, -50.15) * mm});
            skLineSegment(sketch, "E13.33.7", {"start": v(88.1, -50.38) * mm, "end": v(89.24, -50.64) * mm});
            skArc(sketch, "E13.34.0", {"start": v(94.89, -39.06) * mm, "mid": v(96.33, -39.04) * mm, "end": v(97.74, -38.7) * mm});
            skArc(sketch, "E13.34.1", {"start": v(90.58, -48.22) * mm, "mid": v(91.49, -49.34) * mm, "end": v(92.12, -50.64) * mm});
            skLineSegment(sketch, "E13.34.2", {"start": v(89.74, -47.4) * mm, "end": v(90.58, -48.22) * mm});
            skArc(sketch, "E13.34.3", {"start": v(89.74, -47.4) * mm, "mid": v(88.74, -46.24) * mm, "end": v(87.92, -44.95) * mm});
            skArc(sketch, "E13.34.4", {"start": v(87.92, -44.95) * mm, "mid": v(87.43, -43.15) * mm, "end": v(87.81, -41.32) * mm});
            skArc(sketch, "E13.34.5", {"start": v(90.68, -39.09) * mm, "mid": v(88.98, -39.86) * mm, "end": v(87.81, -41.32) * mm});
            skArc(sketch, "E13.34.6", {"start": v(93.72, -38.94) * mm, "mid": v(92.2, -38.9) * mm, "end": v(90.68, -39.09) * mm});
            skLineSegment(sketch, "E13.34.7", {"start": v(93.72, -38.94) * mm, "end": v(94.89, -39.06) * mm});
            skArc(sketch, "E13.35.0", {"start": v(99.03, -26.85) * mm, "mid": v(100.47, -26.66) * mm, "end": v(101.82, -26.14) * mm});
            skArc(sketch, "E13.35.1", {"start": v(95.9, -36.48) * mm, "mid": v(96.95, -37.49) * mm, "end": v(97.74, -38.7) * mm});
            skLineSegment(sketch, "E13.35.2", {"start": v(94.97, -35.78) * mm, "end": v(95.9, -36.48) * mm});
            skArc(sketch, "E13.35.3", {"start": v(94.97, -35.78) * mm, "mid": v(93.84, -34.76) * mm, "end": v(92.86, -33.58) * mm});
            skArc(sketch, "E13.35.4", {"start": v(92.86, -33.58) * mm, "mid": v(92.15, -31.85) * mm, "end": v(92.3, -29.99) * mm});
            skArc(sketch, "E13.35.5", {"start": v(94.86, -27.42) * mm, "mid": v(93.27, -28.4) * mm, "end": v(92.3, -29.99) * mm});
            skArc(sketch, "E13.35.6", {"start": v(97.86, -26.88) * mm, "mid": v(96.34, -27.04) * mm, "end": v(94.86, -27.42) * mm});
            skLineSegment(sketch, "E13.35.7", {"start": v(97.86, -26.88) * mm, "end": v(99.03, -26.85) * mm});
            skArc(sketch, "E13.36.0", {"start": v(101.62, -14.23) * mm, "mid": v(103.02, -13.86) * mm, "end": v(104.3, -13.18) * mm});
            skArc(sketch, "E13.36.1", {"start": v(99.72, -24.18) * mm, "mid": v(100.88, -25.04) * mm, "end": v(101.82, -26.14) * mm});
            skLineSegment(sketch, "E13.36.2", {"start": v(98.7, -23.59) * mm, "end": v(99.72, -24.18) * mm});
            skArc(sketch, "E13.36.3", {"start": v(98.7, -23.59) * mm, "mid": v(97.45, -22.72) * mm, "end": v(96.34, -21.68) * mm});
            skArc(sketch, "E13.36.4", {"start": v(96.34, -21.68) * mm, "mid": v(95.42, -20.05) * mm, "end": v(95.33, -18.19) * mm});
            skArc(sketch, "E13.36.5", {"start": v(97.55, -15.31) * mm, "mid": v(96.1, -16.48) * mm, "end": v(95.33, -18.19) * mm});
            skArc(sketch, "E13.36.6", {"start": v(100.46, -14.4) * mm, "mid": v(98.97, -14.75) * mm, "end": v(97.55, -15.31) * mm});
            skLineSegment(sketch, "E13.36.7", {"start": v(100.46, -14.4) * mm, "end": v(101.62, -14.23) * mm});
            skArc(sketch, "E13.37.0", {"start": v(102.6, -1.38) * mm, "mid": v(103.94, -0.84) * mm, "end": v(105.13, 0) * mm});
            skArc(sketch, "E13.37.1", {"start": v(101.96, -11.49) * mm, "mid": v(103.23, -12.2) * mm, "end": v(104.3, -13.18) * mm});
            skLineSegment(sketch, "E13.37.2", {"start": v(100.89, -11.03) * mm, "end": v(101.96, -11.49) * mm});
            skArc(sketch, "E13.37.3", {"start": v(100.89, -11.03) * mm, "mid": v(99.53, -10.33) * mm, "end": v(98.3, -9.43) * mm});
            skArc(sketch, "E13.37.4", {"start": v(98.3, -9.43) * mm, "mid": v(97.18, -7.93) * mm, "end": v(96.86, -6.1) * mm});
            skArc(sketch, "E13.37.5", {"start": v(98.7, -2.96) * mm, "mid": v(97.4, -4.3) * mm, "end": v(96.86, -6.1) * mm});
            skArc(sketch, "E13.37.6", {"start": v(101.47, -1.7) * mm, "mid": v(100.04, -2.23) * mm, "end": v(98.7, -2.96) * mm});
            skLineSegment(sketch, "E13.37.7", {"start": v(101.47, -1.7) * mm, "end": v(102.6, -1.38) * mm});
            skArc(sketch, "E13.38.0", {"start": v(101.96, 11.49) * mm, "mid": v(103.23, 12.2) * mm, "end": v(104.3, 13.18) * mm});
            skArc(sketch, "E13.38.1", {"start": v(102.6, 1.38) * mm, "mid": v(103.94, 0.84) * mm, "end": v(105.13, 0) * mm});
            skLineSegment(sketch, "E13.38.2", {"start": v(101.47, 1.7) * mm, "end": v(102.6, 1.38) * mm});
            skArc(sketch, "E13.38.3", {"start": v(101.47, 1.7) * mm, "mid": v(100.04, 2.23) * mm, "end": v(98.7, 2.96) * mm});
            skArc(sketch, "E13.38.4", {"start": v(98.7, 2.96) * mm, "mid": v(97.4, 4.3) * mm, "end": v(96.86, 6.1) * mm});
            skArc(sketch, "E13.38.5", {"start": v(98.3, 9.43) * mm, "mid": v(97.18, 7.93) * mm, "end": v(96.86, 6.1) * mm});
            skArc(sketch, "E13.38.6", {"start": v(100.89, 11.03) * mm, "mid": v(99.53, 10.33) * mm, "end": v(98.3, 9.43) * mm});
            skLineSegment(sketch, "E13.38.7", {"start": v(100.89, 11.03) * mm, "end": v(101.96, 11.49) * mm});
            skArc(sketch, "E13.39.0", {"start": v(99.72, 24.18) * mm, "mid": v(100.88, 25.04) * mm, "end": v(101.82, 26.14) * mm});
            skArc(sketch, "E13.39.1", {"start": v(101.62, 14.23) * mm, "mid": v(103.02, 13.86) * mm, "end": v(104.3, 13.18) * mm});
            skLineSegment(sketch, "E13.39.2", {"start": v(100.46, 14.4) * mm, "end": v(101.62, 14.23) * mm});
            skArc(sketch, "E13.39.3", {"start": v(100.46, 14.4) * mm, "mid": v(98.97, 14.75) * mm, "end": v(97.55, 15.31) * mm});
            skArc(sketch, "E13.39.4", {"start": v(97.55, 15.31) * mm, "mid": v(96.1, 16.48) * mm, "end": v(95.33, 18.19) * mm});
            skArc(sketch, "E13.39.5", {"start": v(96.34, 21.68) * mm, "mid": v(95.42, 20.05) * mm, "end": v(95.33, 18.19) * mm});
            skArc(sketch, "E13.39.6", {"start": v(98.7, 23.59) * mm, "mid": v(97.45, 22.72) * mm, "end": v(96.34, 21.68) * mm});
            skLineSegment(sketch, "E13.39.7", {"start": v(98.7, 23.59) * mm, "end": v(99.72, 24.18) * mm});
            skArc(sketch, "E13.40.0", {"start": v(95.9, 36.48) * mm, "mid": v(96.95, 37.49) * mm, "end": v(97.74, 38.7) * mm});
            skArc(sketch, "E13.40.1", {"start": v(99.03, 26.85) * mm, "mid": v(100.47, 26.66) * mm, "end": v(101.82, 26.14) * mm});
            skLineSegment(sketch, "E13.40.2", {"start": v(97.86, 26.88) * mm, "end": v(99.03, 26.85) * mm});
            skArc(sketch, "E13.40.3", {"start": v(97.86, 26.88) * mm, "mid": v(96.34, 27.04) * mm, "end": v(94.86, 27.42) * mm});
            skArc(sketch, "E13.40.4", {"start": v(94.86, 27.42) * mm, "mid": v(93.27, 28.4) * mm, "end": v(92.3, 29.99) * mm});
            skArc(sketch, "E13.40.5", {"start": v(92.86, 33.58) * mm, "mid": v(92.15, 31.85) * mm, "end": v(92.3, 29.99) * mm});
            skArc(sketch, "E13.40.6", {"start": v(94.97, 35.78) * mm, "mid": v(93.84, 34.76) * mm, "end": v(92.86, 33.58) * mm});
            skLineSegment(sketch, "E13.40.7", {"start": v(94.97, 35.78) * mm, "end": v(95.9, 36.48) * mm});
            skArc(sketch, "E13.41.0", {"start": v(90.58, 48.22) * mm, "mid": v(91.49, 49.34) * mm, "end": v(92.12, 50.64) * mm});
            skArc(sketch, "E13.41.1", {"start": v(94.89, 39.06) * mm, "mid": v(96.33, 39.04) * mm, "end": v(97.74, 38.7) * mm});
            skLineSegment(sketch, "E13.41.2", {"start": v(93.72, 38.94) * mm, "end": v(94.89, 39.06) * mm});
            skArc(sketch, "E13.41.3", {"start": v(93.72, 38.94) * mm, "mid": v(92.2, 38.9) * mm, "end": v(90.68, 39.09) * mm});
            skArc(sketch, "E13.41.4", {"start": v(90.68, 39.09) * mm, "mid": v(88.98, 39.86) * mm, "end": v(87.81, 41.32) * mm});
            skArc(sketch, "E13.41.5", {"start": v(87.92, 44.95) * mm, "mid": v(87.43, 43.15) * mm, "end": v(87.81, 41.32) * mm});
            skArc(sketch, "E13.41.6", {"start": v(89.74, 47.4) * mm, "mid": v(88.74, 46.24) * mm, "end": v(87.92, 44.95) * mm});
            skLineSegment(sketch, "E13.41.7", {"start": v(89.74, 47.4) * mm, "end": v(90.58, 48.22) * mm});
            skArc(sketch, "E13.42.0", {"start": v(83.82, 59.19) * mm, "mid": v(84.58, 60.42) * mm, "end": v(85.05, 61.8) * mm});
            skArc(sketch, "E13.42.1", {"start": v(89.24, 50.64) * mm, "mid": v(90.68, 50.8) * mm, "end": v(92.12, 50.64) * mm});
            skLineSegment(sketch, "E13.42.2", {"start": v(88.1, 50.38) * mm, "end": v(89.24, 50.64) * mm});
            skArc(sketch, "E13.42.3", {"start": v(88.1, 50.38) * mm, "mid": v(86.6, 50.15) * mm, "end": v(85.06, 50.15) * mm});
            skArc(sketch, "E13.42.4", {"start": v(85.06, 50.15) * mm, "mid": v(83.28, 50.7) * mm, "end": v(81.94, 52) * mm});
            skArc(sketch, "E13.42.5", {"start": v(81.6, 55.62) * mm, "mid": v(81.33, 53.77) * mm, "end": v(81.94, 52) * mm});
            skArc(sketch, "E13.42.6", {"start": v(83.1, 58.27) * mm, "mid": v(82.25, 57) * mm, "end": v(81.6, 55.62) * mm});
            skLineSegment(sketch, "E13.42.7", {"start": v(83.1, 58.27) * mm, "end": v(83.82, 59.19) * mm});
            skArc(sketch, "E13.43.0", {"start": v(75.74, 69.23) * mm, "mid": v(76.34, 70.54) * mm, "end": v(76.63, 71.96) * mm});
            skArc(sketch, "E13.43.1", {"start": v(82.2, 61.43) * mm, "mid": v(83.6, 61.77) * mm, "end": v(85.05, 61.8) * mm});
            skLineSegment(sketch, "E13.43.2", {"start": v(81.1, 61.02) * mm, "end": v(82.2, 61.43) * mm});
            skArc(sketch, "E13.43.3", {"start": v(81.1, 61.02) * mm, "mid": v(79.62, 60.6) * mm, "end": v(78.1, 60.41) * mm});
            skArc(sketch, "E13.43.4", {"start": v(78.1, 60.41) * mm, "mid": v(76.27, 60.74) * mm, "end": v(74.78, 61.86) * mm});
            skArc(sketch, "E13.43.5", {"start": v(73.98, 65.4) * mm, "mid": v(73.95, 63.54) * mm, "end": v(74.78, 61.86) * mm});
            skArc(sketch, "E13.43.6", {"start": v(75.14, 68.23) * mm, "mid": v(74.45, 66.86) * mm, "end": v(73.98, 65.4) * mm});
            skLineSegment(sketch, "E13.43.7", {"start": v(75.14, 68.23) * mm, "end": v(75.74, 69.23) * mm});
            skArc(sketch, "E13.44.0", {"start": v(66.47, 78.17) * mm, "mid": v(66.9, 79.56) * mm, "end": v(67, 81) * mm});
            skArc(sketch, "E13.44.1", {"start": v(73.85, 71.24) * mm, "mid": v(75.2, 71.76) * mm, "end": v(76.63, 71.96) * mm});
            skLineSegment(sketch, "E13.44.2", {"start": v(72.8, 70.7) * mm, "end": v(73.85, 71.24) * mm});
            skArc(sketch, "E13.44.3", {"start": v(72.8, 70.7) * mm, "mid": v(71.4, 70.1) * mm, "end": v(69.92, 69.73) * mm});
            skArc(sketch, "E13.44.4", {"start": v(69.92, 69.73) * mm, "mid": v(68.06, 69.82) * mm, "end": v(66.43, 70.75) * mm});
            skArc(sketch, "E13.44.5", {"start": v(65.2, 74.16) * mm, "mid": v(65.4, 72.3) * mm, "end": v(66.43, 70.75) * mm});
            skArc(sketch, "E13.44.6", {"start": v(66, 77.1) * mm, "mid": v(65.49, 75.66) * mm, "end": v(65.2, 74.16) * mm});
            skLineSegment(sketch, "E13.44.7", {"start": v(66, 77.1) * mm, "end": v(66.47, 78.17) * mm});
            skArc(sketch, "E13.45.0", {"start": v(56.14, 85.89) * mm, "mid": v(56.4, 87.31) * mm, "end": v(56.33, 88.76) * mm});
            skArc(sketch, "E13.45.1", {"start": v(64.33, 79.94) * mm, "mid": v(65.61, 80.62) * mm, "end": v(67, 81) * mm});
            skLineSegment(sketch, "E13.45.2", {"start": v(63.37, 79.27) * mm, "end": v(64.33, 79.94) * mm});
            skArc(sketch, "E13.45.3", {"start": v(63.37, 79.27) * mm, "mid": v(62.05, 78.5) * mm, "end": v(60.63, 77.94) * mm});
            skArc(sketch, "E13.45.4", {"start": v(60.63, 77.94) * mm, "mid": v(58.77, 77.8) * mm, "end": v(57.04, 78.51) * mm});
            skArc(sketch, "E13.45.5", {"start": v(55.39, 81.75) * mm, "mid": v(55.83, 79.93) * mm, "end": v(57.04, 78.51) * mm});
            skArc(sketch, "E13.45.6", {"start": v(55.8, 84.77) * mm, "mid": v(55.49, 83.27) * mm, "end": v(55.39, 81.75) * mm});
            skLineSegment(sketch, "E13.45.7", {"start": v(55.8, 84.77) * mm, "end": v(56.14, 85.89) * mm});
            skArc(sketch, "E13.46.0", {"start": v(44.94, 92.25) * mm, "mid": v(45.01, 93.7) * mm, "end": v(44.76, 95.12) * mm});
            skArc(sketch, "E13.46.1", {"start": v(53.8, 87.37) * mm, "mid": v(54.99, 88.2) * mm, "end": v(56.33, 88.76) * mm});
            skLineSegment(sketch, "E13.46.2", {"start": v(52.94, 86.59) * mm, "end": v(53.8, 87.37) * mm});
            skArc(sketch, "E13.46.3", {"start": v(52.94, 86.59) * mm, "mid": v(51.72, 85.66) * mm, "end": v(50.38, 84.92) * mm});
            skArc(sketch, "E13.46.4", {"start": v(50.38, 84.92) * mm, "mid": v(48.55, 84.55) * mm, "end": v(46.75, 85.04) * mm});
            skArc(sketch, "E13.46.5", {"start": v(44.7, 88.05) * mm, "mid": v(45.37, 86.3) * mm, "end": v(46.75, 85.04) * mm});
            skArc(sketch, "E13.46.6", {"start": v(44.74, 91.1) * mm, "mid": v(44.61, 89.57) * mm, "end": v(44.7, 88.05) * mm});
            skLineSegment(sketch, "E13.46.7", {"start": v(44.74, 91.1) * mm, "end": v(44.94, 92.25) * mm});
            skArc(sketch, "E13.47.0", {"start": v(33.02, 97.15) * mm, "mid": v(32.91, 98.6) * mm, "end": v(32.49, 99.98) * mm});
            skArc(sketch, "E13.47.1", {"start": v(42.43, 93.42) * mm, "mid": v(43.5, 94.4) * mm, "end": v(44.76, 95.12) * mm});
            skLineSegment(sketch, "E13.47.2", {"start": v(41.67, 92.54) * mm, "end": v(42.43, 93.42) * mm});
            skArc(sketch, "E13.47.3", {"start": v(41.67, 92.54) * mm, "mid": v(40.58, 91.47) * mm, "end": v(39.34, 90.57) * mm});
            skArc(sketch, "E13.47.4", {"start": v(39.34, 90.57) * mm, "mid": v(37.57, 89.97) * mm, "end": v(35.73, 90.23) * mm});
            skArc(sketch, "E13.47.5", {"start": v(33.32, 92.95) * mm, "mid": v(34.2, 91.3) * mm, "end": v(35.73, 90.23) * mm});
            skArc(sketch, "E13.47.6", {"start": v(32.97, 95.98) * mm, "mid": v(33.03, 94.46) * mm, "end": v(33.32, 92.95) * mm});
            skLineSegment(sketch, "E13.47.7", {"start": v(32.97, 95.98) * mm, "end": v(33.02, 97.15) * mm});
            skArc(sketch, "E13.48.0", {"start": v(20.58, 100.52) * mm, "mid": v(20.3, 101.94) * mm, "end": v(19.7, 103.26) * mm});
            skArc(sketch, "E13.48.1", {"start": v(30.39, 98) * mm, "mid": v(31.33, 99.11) * mm, "end": v(32.49, 99.98) * mm});
            skLineSegment(sketch, "E13.48.2", {"start": v(29.74, 97.03) * mm, "end": v(30.39, 98) * mm});
            skArc(sketch, "E13.48.3", {"start": v(29.74, 97.03) * mm, "mid": v(28.8, 95.83) * mm, "end": v(27.68, 94.79) * mm});
            skArc(sketch, "E13.48.4", {"start": v(27.68, 94.79) * mm, "mid": v(26, 93.97) * mm, "end": v(24.13, 94) * mm});
            skArc(sketch, "E13.48.5", {"start": v(21.4, 96.4) * mm, "mid": v(22.48, 94.87) * mm, "end": v(24.13, 94) * mm});
            skArc(sketch, "E13.48.6", {"start": v(20.68, 99.36) * mm, "mid": v(20.94, 97.85) * mm, "end": v(21.4, 96.4) * mm});
            skLineSegment(sketch, "E13.48.7", {"start": v(20.68, 99.36) * mm, "end": v(20.58, 100.52) * mm});
            skArc(sketch, "E13.49.0", {"start": v(7.82, 102.31) * mm, "mid": v(7.36, 103.68) * mm, "end": v(6.6, 104.92) * mm});
            skArc(sketch, "E13.49.1", {"start": v(17.87, 101.04) * mm, "mid": v(18.66, 102.26) * mm, "end": v(19.7, 103.26) * mm});
            skLineSegment(sketch, "E13.49.2", {"start": v(17.35, 100) * mm, "end": v(17.87, 101.04) * mm});
            skArc(sketch, "E13.49.3", {"start": v(17.35, 100) * mm, "mid": v(16.56, 98.69) * mm, "end": v(15.58, 97.5) * mm});
            skArc(sketch, "E13.49.4", {"start": v(15.58, 97.5) * mm, "mid": v(14.02, 96.49) * mm, "end": v(12.16, 96.28) * mm});
            skArc(sketch, "E13.49.5", {"start": v(9.15, 98.32) * mm, "mid": v(10.42, 96.94) * mm, "end": v(12.16, 96.28) * mm});
            skArc(sketch, "E13.49.6", {"start": v(8.07, 101.17) * mm, "mid": v(8.5, 99.7) * mm, "end": v(9.15, 98.32) * mm});
            skLineSegment(sketch, "E13.49.7", {"start": v(8.07, 101.17) * mm, "end": v(7.82, 102.31) * mm});
            skCircle(sketch, "E14", {"center": v(0, 0) * mm, "radius": 103.5 * mm});
            skCircle(sketch, "E15", {"center": v(0, -65) * mm, "radius": 5 * mm});
            skSolve(sketch);
        }
        {
            var Q0;
            Q0=makeQuery(id+"F0.imprint","IMPRINT",FACE,{"disambiguationData":[TD([[makeQuery(id+"F0.imprint","IMPRINT",EDGE,{"derivedFrom":sQuery(id+"F0.wireOp",EDGE,"E2")}),-1.0]])]});
            extrude(context, id + "F1", {"entities" : qUnion([Q0]), "endBound" : BoundingType.SYMMETRIC, "depth" : 4.5 * mm});
        }
        {
            var Q0;
            Q0=makeQuery(id+"F0.imprint","IMPRINT",FACE,{"disambiguationData":[TD([[makeQuery(id+"F0.imprint","IMPRINT",EDGE,{"derivedFrom":sQuery(id+"F0.wireOp",EDGE,"E4")}),-1.0]])]});
            extrude(context, id + "F2", {"entities" : qUnion([Q0]), "operationType" : NewBodyOperationType.ADD, "endBound" : BoundingType.SYMMETRIC, "depth" : 3.5 * mm});
        }
        {
            var Q0;
            {var subQ0=sQuery(id+"F0.wireOp",EDGE,"E15");var subQ1=sQuery(id+"F0.wireOp",EDGE,"E1");Q0=makeQuery(id+"F1.opExtrude","SWEPT_EDGE",EDGE,{"disambiguationData":[OSD([subQ1,subQ0]),TDD([makeQuery(id+"F0.imprint","INTERSECT",VERTEX,{"disambiguationData":[OD(0.0)],"derivedFrom":[subQ1,subQ0]})])]});}
            var Q1;
            {var subQ0=sQuery(id+"F0.wireOp",EDGE,"E15");var subQ1=sQuery(id+"F0.wireOp",EDGE,"E1");Q1=makeQuery(id+"F1.opExtrude","SWEPT_EDGE",EDGE,{"disambiguationData":[OSD([subQ1,subQ0]),TDD([makeQuery(id+"F0.imprint","INTERSECT",VERTEX,{"disambiguationData":[OD(1.0)],"derivedFrom":[subQ1,subQ0]})])]});}
            fillet(context, id + "F3", {"entities" : qUnion([Q0, Q1]), "radius" : 5.08 * mm, "tangentPropagation" : true, "allowEdgeOverflow" : false});
        }
        {
            var Q0;
            Q0=makeQuery(id+"F1.opExtrude","CAP_FACE",FACE,{"disambiguationData":[OSD([sQuery(id+"F0.wireOp",EDGE,"E1"),sQuery(id+"F0.wireOp",EDGE,"E2"),sQuery(id+"F0.wireOp",EDGE,"E3.1.0"),sQuery(id+"F0.wireOp",EDGE,"E3.2.0"),sQuery(id+"F0.wireOp",EDGE,"E3.3.0"),sQuery(id+"F0.wireOp",EDGE,"E3.4.0"),sQuery(id+"F0.wireOp",EDGE,"E4"),sQuery(id+"F0.wireOp",EDGE,"E15")])],"isStart":false});
            var sketch = newSketch(context, id + "F4", { "sketchPlane" : qUnion([Q0])});
            skLineSegment(sketch, "E16", {"start": v(48.72, -50.37) * mm, "end": v(62.2, -64.3) * mm});
            skLineSegment(sketch, "E17", {"start": v(69.03, 12.11) * mm, "end": v(88.12, 15.46) * mm});
            skArc(sketch, "E18", {"start": v(48.72, -50.37) * mm, "mid": v(52.15, -46.82) * mm, "end": v(55.31, -43.03) * mm});
            skArc(sketch, "E19", {"start": v(62.2, -64.3) * mm, "mid": v(66.57, -59.77) * mm, "end": v(70.61, -54.94) * mm});
            skLineSegment(sketch, "E20", {"start": v(70.04, 2.3) * mm, "end": v(89.42, 2.94) * mm});
            skLineSegment(sketch, "E21", {"start": v(70.08, 0.47) * mm, "end": v(89.47, 0.6) * mm});
            skLineSegment(sketch, "E22", {"start": v(69.45, -9.37) * mm, "end": v(88.67, -11.96) * mm});
            skLineSegment(sketch, "E23", {"start": v(69.18, -11.18) * mm, "end": v(88.32, -14.28) * mm});
            skLineSegment(sketch, "E24", {"start": v(66.93, -20.78) * mm, "end": v(85.44, -26.53) * mm});
            skLineSegment(sketch, "E25", {"start": v(66.36, -22.53) * mm, "end": v(84.72, -28.76) * mm});
            skLineSegment(sketch, "E26", {"start": v(62.54, -31.62) * mm, "end": v(79.85, -40.36) * mm});
            skLineSegment(sketch, "E27", {"start": v(61.7, -33.24) * mm, "end": v(78.76, -42.44) * mm});
            skLineSegment(sketch, "E28", {"start": v(56.42, -41.57) * mm, "end": v(72.03, -53.07) * mm});
            skLineSegment(sketch, "E29", {"start": v(55.31, -43.03) * mm, "end": v(70.61, -54.94) * mm});
            skArc(sketch, "E30.trimOffspring", {"start": v(72.03, -53.07) * mm, "mid": v(75.58, -47.87) * mm, "end": v(78.76, -42.44) * mm});
            skArc(sketch, "E31.trimOffspring", {"start": v(79.85, -40.36) * mm, "mid": v(82.49, -34.65) * mm, "end": v(84.72, -28.76) * mm});
            skArc(sketch, "E32.trimOffspring", {"start": v(85.44, -26.53) * mm, "mid": v(87.1, -20.45) * mm, "end": v(88.32, -14.28) * mm});
            skArc(sketch, "E33.trimOffspring", {"start": v(88.67, -11.96) * mm, "mid": v(89.29, -5.7) * mm, "end": v(89.47, 0.6) * mm});
            skArc(sketch, "E34.trimOffspring", {"start": v(89.42, 2.94) * mm, "mid": v(89, 9.23) * mm, "end": v(88.12, 15.46) * mm});
            skArc(sketch, "E35.trimOffspring", {"start": v(70.04, 2.3) * mm, "mid": v(69.7, 7.23) * mm, "end": v(69.03, 12.11) * mm});
            skArc(sketch, "E36.trimOffspring", {"start": v(69.45, -9.37) * mm, "mid": v(69.94, -4.46) * mm, "end": v(70.08, 0.47) * mm});
            skArc(sketch, "E37.trimOffspring", {"start": v(66.93, -20.78) * mm, "mid": v(68.22, -16.02) * mm, "end": v(69.18, -11.18) * mm});
            skArc(sketch, "E38.trimOffspring", {"start": v(62.54, -31.62) * mm, "mid": v(64.61, -27.14) * mm, "end": v(66.36, -22.53) * mm});
            skArc(sketch, "E39.trimOffspring", {"start": v(56.42, -41.57) * mm, "mid": v(59.2, -37.5) * mm, "end": v(61.7, -33.24) * mm});
            skLineSegment(sketch, "E40.1.0", {"start": v(9.81, 69.39) * mm, "end": v(12.53, 88.59) * mm});
            skLineSegment(sketch, "E40.1.1", {"start": v(19.45, 67.33) * mm, "end": v(24.83, 85.95) * mm});
            skLineSegment(sketch, "E40.1.2", {"start": v(21.2, 66.8) * mm, "end": v(27.08, 85.27) * mm});
            skLineSegment(sketch, "E40.1.3", {"start": v(32.01, 62.34) * mm, "end": v(40.87, 79.59) * mm});
            skLineSegment(sketch, "E40.1.4", {"start": v(30.37, 63.16) * mm, "end": v(38.77, 80.63) * mm});
            skArc(sketch, "E40.1.5", {"start": v(38.77, 80.63) * mm, "mid": v(33, 83.16) * mm, "end": v(27.08, 85.27) * mm});
            skArc(sketch, "E40.1.6", {"start": v(24.83, 85.95) * mm, "mid": v(18.73, 87.49) * mm, "end": v(12.53, 88.59) * mm});
            skArc(sketch, "E40.1.7", {"start": v(19.45, 67.33) * mm, "mid": v(14.67, 68.53) * mm, "end": v(9.81, 69.39) * mm});
            skArc(sketch, "E40.1.8", {"start": v(30.37, 63.16) * mm, "mid": v(25.85, 65.14) * mm, "end": v(21.2, 66.8) * mm});
            skArc(sketch, "E40.1.9", {"start": v(40.45, 57.23) * mm, "mid": v(36.32, 59.93) * mm, "end": v(32.01, 62.34) * mm});
            skArc(sketch, "E40.1.10", {"start": v(49.4, 49.71) * mm, "mid": v(45.78, 53.06) * mm, "end": v(41.93, 56.15) * mm});
            skArc(sketch, "E40.1.11", {"start": v(56.97, 40.81) * mm, "mid": v(53.96, 44.72) * mm, "end": v(50.68, 48.4) * mm});
            skArc(sketch, "E40.1.12", {"start": v(62.96, 30.77) * mm, "mid": v(60.64, 35.13) * mm, "end": v(58.02, 39.3) * mm});
            skArc(sketch, "E40.1.13", {"start": v(80.38, 39.29) * mm, "mid": v(77.42, 44.84) * mm, "end": v(74.07, 50.18) * mm});
            skLineSegment(sketch, "E40.1.14", {"start": v(62.96, 30.77) * mm, "end": v(80.38, 39.29) * mm});
            skLineSegment(sketch, "E40.1.15", {"start": v(58.02, 39.3) * mm, "end": v(74.07, 50.18) * mm});
            skLineSegment(sketch, "E40.1.16", {"start": v(56.97, 40.81) * mm, "end": v(72.73, 52.1) * mm});
            skArc(sketch, "E40.1.17", {"start": v(72.73, 52.1) * mm, "mid": v(68.89, 57.09) * mm, "end": v(64.7, 61.8) * mm});
            skLineSegment(sketch, "E40.1.18", {"start": v(50.68, 48.4) * mm, "end": v(64.7, 61.8) * mm});
            skArc(sketch, "E40.1.19", {"start": v(63.06, 63.46) * mm, "mid": v(58.44, 67.74) * mm, "end": v(53.53, 71.69) * mm});
            skLineSegment(sketch, "E40.1.20", {"start": v(49.4, 49.71) * mm, "end": v(63.06, 63.46) * mm});
            skLineSegment(sketch, "E40.1.21", {"start": v(41.93, 56.15) * mm, "end": v(53.53, 71.69) * mm});
            skArc(sketch, "E40.1.22", {"start": v(51.64, 73.06) * mm, "mid": v(46.37, 76.51) * mm, "end": v(40.87, 79.59) * mm});
            skLineSegment(sketch, "E40.1.23", {"start": v(40.45, 57.23) * mm, "end": v(51.64, 73.06) * mm});
            skLineSegment(sketch, "E40.2.0", {"start": v(-62.96, 30.77) * mm, "end": v(-80.38, 39.29) * mm});
            skLineSegment(sketch, "E40.2.1", {"start": v(-58.02, 39.3) * mm, "end": v(-74.07, 50.18) * mm});
            skLineSegment(sketch, "E40.2.2", {"start": v(-56.97, 40.81) * mm, "end": v(-72.73, 52.1) * mm});
            skLineSegment(sketch, "E40.2.3", {"start": v(-49.4, 49.71) * mm, "end": v(-63.06, 63.46) * mm});
            skLineSegment(sketch, "E40.2.4", {"start": v(-50.68, 48.4) * mm, "end": v(-64.7, 61.8) * mm});
            skArc(sketch, "E40.2.5", {"start": v(-64.7, 61.8) * mm, "mid": v(-68.89, 57.09) * mm, "end": v(-72.73, 52.1) * mm});
            skArc(sketch, "E40.2.6", {"start": v(-74.07, 50.18) * mm, "mid": v(-77.42, 44.84) * mm, "end": v(-80.38, 39.29) * mm});
            skArc(sketch, "E40.2.7", {"start": v(-58.02, 39.3) * mm, "mid": v(-60.64, 35.13) * mm, "end": v(-62.96, 30.77) * mm});
            skArc(sketch, "E40.2.8", {"start": v(-50.68, 48.4) * mm, "mid": v(-53.96, 44.72) * mm, "end": v(-56.97, 40.81) * mm});
            skArc(sketch, "E40.2.9", {"start": v(-41.93, 56.15) * mm, "mid": v(-45.78, 53.06) * mm, "end": v(-49.4, 49.71) * mm});
            skArc(sketch, "E40.2.10", {"start": v(-32.01, 62.34) * mm, "mid": v(-36.32, 59.93) * mm, "end": v(-40.45, 57.23) * mm});
            skArc(sketch, "E40.2.11", {"start": v(-21.2, 66.8) * mm, "mid": v(-25.85, 65.14) * mm, "end": v(-30.37, 63.16) * mm});
            skArc(sketch, "E40.2.12", {"start": v(-9.81, 69.39) * mm, "mid": v(-14.67, 68.53) * mm, "end": v(-19.45, 67.33) * mm});
            skArc(sketch, "E40.2.13", {"start": v(-12.53, 88.59) * mm, "mid": v(-18.73, 87.49) * mm, "end": v(-24.83, 85.95) * mm});
            skLineSegment(sketch, "E40.2.14", {"start": v(-9.81, 69.39) * mm, "end": v(-12.53, 88.59) * mm});
            skLineSegment(sketch, "E40.2.15", {"start": v(-19.45, 67.33) * mm, "end": v(-24.83, 85.95) * mm});
            skLineSegment(sketch, "E40.2.16", {"start": v(-21.2, 66.8) * mm, "end": v(-27.08, 85.27) * mm});
            skArc(sketch, "E40.2.17", {"start": v(-27.08, 85.27) * mm, "mid": v(-33, 83.16) * mm, "end": v(-38.77, 80.63) * mm});
            skLineSegment(sketch, "E40.2.18", {"start": v(-30.37, 63.16) * mm, "end": v(-38.77, 80.63) * mm});
            skArc(sketch, "E40.2.19", {"start": v(-40.87, 79.59) * mm, "mid": v(-46.37, 76.51) * mm, "end": v(-51.64, 73.06) * mm});
            skLineSegment(sketch, "E40.2.20", {"start": v(-32.01, 62.34) * mm, "end": v(-40.87, 79.59) * mm});
            skLineSegment(sketch, "E40.2.21", {"start": v(-40.45, 57.23) * mm, "end": v(-51.64, 73.06) * mm});
            skArc(sketch, "E40.2.22", {"start": v(-53.53, 71.69) * mm, "mid": v(-58.44, 67.74) * mm, "end": v(-63.06, 63.46) * mm});
            skLineSegment(sketch, "E40.2.23", {"start": v(-41.93, 56.15) * mm, "end": v(-53.53, 71.69) * mm});
            skLineSegment(sketch, "E40.3.0", {"start": v(-48.72, -50.37) * mm, "end": v(-62.2, -64.3) * mm});
            skLineSegment(sketch, "E40.3.1", {"start": v(-55.31, -43.03) * mm, "end": v(-70.61, -54.94) * mm});
            skLineSegment(sketch, "E40.3.2", {"start": v(-56.42, -41.57) * mm, "end": v(-72.03, -53.07) * mm});
            skLineSegment(sketch, "E40.3.3", {"start": v(-62.54, -31.62) * mm, "end": v(-79.85, -40.36) * mm});
            skLineSegment(sketch, "E40.3.4", {"start": v(-61.7, -33.24) * mm, "end": v(-78.76, -42.44) * mm});
            skArc(sketch, "E40.3.5", {"start": v(-78.76, -42.44) * mm, "mid": v(-75.58, -47.87) * mm, "end": v(-72.03, -53.07) * mm});
            skArc(sketch, "E40.3.6", {"start": v(-70.61, -54.94) * mm, "mid": v(-66.57, -59.77) * mm, "end": v(-62.2, -64.3) * mm});
            skArc(sketch, "E40.3.7", {"start": v(-55.31, -43.03) * mm, "mid": v(-52.15, -46.82) * mm, "end": v(-48.72, -50.37) * mm});
            skArc(sketch, "E40.3.8", {"start": v(-61.7, -33.24) * mm, "mid": v(-59.2, -37.5) * mm, "end": v(-56.42, -41.57) * mm});
            skArc(sketch, "E40.3.9", {"start": v(-66.36, -22.53) * mm, "mid": v(-64.61, -27.14) * mm, "end": v(-62.54, -31.62) * mm});
            skArc(sketch, "E40.3.10", {"start": v(-69.18, -11.18) * mm, "mid": v(-68.22, -16.02) * mm, "end": v(-66.93, -20.78) * mm});
            skArc(sketch, "E40.3.11", {"start": v(-70.08, 0.47) * mm, "mid": v(-69.94, -4.46) * mm, "end": v(-69.45, -9.37) * mm});
            skArc(sketch, "E40.3.12", {"start": v(-69.03, 12.11) * mm, "mid": v(-69.7, 7.23) * mm, "end": v(-70.04, 2.3) * mm});
            skArc(sketch, "E40.3.13", {"start": v(-88.12, 15.46) * mm, "mid": v(-89, 9.23) * mm, "end": v(-89.42, 2.94) * mm});
            skLineSegment(sketch, "E40.3.14", {"start": v(-69.03, 12.11) * mm, "end": v(-88.12, 15.46) * mm});
            skLineSegment(sketch, "E40.3.15", {"start": v(-70.04, 2.3) * mm, "end": v(-89.42, 2.94) * mm});
            skLineSegment(sketch, "E40.3.16", {"start": v(-70.08, 0.47) * mm, "end": v(-89.47, 0.6) * mm});
            skArc(sketch, "E40.3.17", {"start": v(-89.47, 0.6) * mm, "mid": v(-89.29, -5.7) * mm, "end": v(-88.67, -11.96) * mm});
            skLineSegment(sketch, "E40.3.18", {"start": v(-69.45, -9.37) * mm, "end": v(-88.67, -11.96) * mm});
            skArc(sketch, "E40.3.19", {"start": v(-88.32, -14.28) * mm, "mid": v(-87.1, -20.45) * mm, "end": v(-85.44, -26.53) * mm});
            skLineSegment(sketch, "E40.3.20", {"start": v(-69.18, -11.18) * mm, "end": v(-88.32, -14.28) * mm});
            skLineSegment(sketch, "E40.3.21", {"start": v(-66.93, -20.78) * mm, "end": v(-85.44, -26.53) * mm});
            skArc(sketch, "E40.3.22", {"start": v(-84.72, -28.76) * mm, "mid": v(-82.49, -34.65) * mm, "end": v(-79.85, -40.36) * mm});
            skLineSegment(sketch, "E40.3.23", {"start": v(-66.36, -22.53) * mm, "end": v(-84.72, -28.76) * mm});
            skSolve(sketch);
        }
        {
            var Q0;
            Q0=makeQuery(id+"F4.imprint","IMPRINT",FACE,{"disambiguationData":[TD([[makeQuery(id+"F4.imprint","IMPRINT",EDGE,{"derivedFrom":sQuery(id+"F4.wireOp",EDGE,"E40.2.0")}),-1.0]])]});
            var Q1;
            Q1=makeQuery(id+"F4.imprint","IMPRINT",FACE,{"disambiguationData":[TD([[makeQuery(id+"F4.imprint","IMPRINT",EDGE,{"derivedFrom":sQuery(id+"F4.wireOp",EDGE,"E40.2.2")}),-1.0]])]});
            var Q2;
            Q2=makeQuery(id+"F4.imprint","IMPRINT",FACE,{"disambiguationData":[TD([[makeQuery(id+"F4.imprint","IMPRINT",EDGE,{"derivedFrom":sQuery(id+"F4.wireOp",EDGE,"E40.3.0")}),-1.0]])]});
            var Q3;
            Q3=makeQuery(id+"F4.imprint","IMPRINT",FACE,{"disambiguationData":[TD([[makeQuery(id+"F4.imprint","IMPRINT",EDGE,{"derivedFrom":sQuery(id+"F4.wireOp",EDGE,"E40.3.2")}),-1.0]])]});
            var Q4;
            Q4=makeQuery(id+"F4.imprint","IMPRINT",FACE,{"disambiguationData":[TD([[makeQuery(id+"F4.imprint","IMPRINT",EDGE,{"derivedFrom":sQuery(id+"F4.wireOp",EDGE,"E40.1.0")}),-1.0]])]});
            var Q5;
            Q5=makeQuery(id+"F4.imprint","IMPRINT",FACE,{"disambiguationData":[TD([[makeQuery(id+"F4.imprint","IMPRINT",EDGE,{"derivedFrom":sQuery(id+"F4.wireOp",EDGE,"E40.1.2")}),-1.0]])]});
            var Q6;
            Q6=makeQuery(id+"F4.imprint","IMPRINT",FACE,{"disambiguationData":[TD([[makeQuery(id+"F4.imprint","IMPRINT",EDGE,{"derivedFrom":sQuery(id+"F4.wireOp",EDGE,"E17")}),-1.0]])]});
            var Q7;
            Q7=makeQuery(id+"F4.imprint","IMPRINT",FACE,{"disambiguationData":[TD([[makeQuery(id+"F4.imprint","IMPRINT",EDGE,{"derivedFrom":sQuery(id+"F4.wireOp",EDGE,"E21")}),-1.0]])]});
            var Q8;
            Q8=makeQuery(id+"F4.imprint","IMPRINT",FACE,{"disambiguationData":[TD([[makeQuery(id+"F4.imprint","IMPRINT",EDGE,{"derivedFrom":sQuery(id+"F4.wireOp",EDGE,"E40.3.11")}),-1.0]])]});
            var Q9;
            Q9=makeQuery(id+"F4.imprint","IMPRINT",FACE,{"disambiguationData":[TD([[makeQuery(id+"F4.imprint","IMPRINT",EDGE,{"derivedFrom":sQuery(id+"F4.wireOp",EDGE,"E40.2.11")}),-1.0]])]});
            var Q10;
            Q10=makeQuery(id+"F4.imprint","IMPRINT",FACE,{"disambiguationData":[TD([[makeQuery(id+"F4.imprint","IMPRINT",EDGE,{"derivedFrom":sQuery(id+"F4.wireOp",EDGE,"E40.1.11")}),-1.0]])]});
            var Q11;
            Q11=makeQuery(id+"F4.imprint","IMPRINT",FACE,{"disambiguationData":[TD([[makeQuery(id+"F4.imprint","IMPRINT",EDGE,{"derivedFrom":sQuery(id+"F4.wireOp",EDGE,"E27")}),-1.0]])]});
            extrude(context, id + "F5", {"entities" : qUnion([Q0, Q1, Q2, Q3, Q4, Q5, Q6, Q7, Q8, Q9, Q10, Q11]), "operationType" : NewBodyOperationType.REMOVE, "oppositeDirection" : true, "depth" : 4.5 * mm});
        }
        {
            var Q0;
            Q0=makeQuery(id+"F4.imprint","IMPRINT",FACE,{"disambiguationData":[TD([[makeQuery(id+"F4.imprint","IMPRINT",EDGE,{"derivedFrom":sQuery(id+"F4.wireOp",EDGE,"E40.3.3")}),-1.0]])]});
            var Q1;
            Q1=makeQuery(id+"F4.imprint","IMPRINT",FACE,{"disambiguationData":[TD([[makeQuery(id+"F4.imprint","IMPRINT",EDGE,{"derivedFrom":sQuery(id+"F4.wireOp",EDGE,"E40.3.12")}),-1.0]])]});
            var Q2;
            Q2=makeQuery(id+"F4.imprint","IMPRINT",FACE,{"disambiguationData":[TD([[makeQuery(id+"F4.imprint","IMPRINT",EDGE,{"derivedFrom":sQuery(id+"F4.wireOp",EDGE,"E40.2.3")}),-1.0]])]});
            var Q3;
            Q3=makeQuery(id+"F4.imprint","IMPRINT",FACE,{"disambiguationData":[TD([[makeQuery(id+"F4.imprint","IMPRINT",EDGE,{"derivedFrom":sQuery(id+"F4.wireOp",EDGE,"E40.2.10")}),-1.0]])]});
            var Q4;
            Q4=makeQuery(id+"F4.imprint","IMPRINT",FACE,{"disambiguationData":[TD([[makeQuery(id+"F4.imprint","IMPRINT",EDGE,{"derivedFrom":sQuery(id+"F4.wireOp",EDGE,"E40.3.10")}),-1.0]])]});
            var Q5;
            Q5=makeQuery(id+"F4.imprint","IMPRINT",FACE,{"disambiguationData":[TD([[makeQuery(id+"F4.imprint","IMPRINT",EDGE,{"derivedFrom":sQuery(id+"F4.wireOp",EDGE,"E40.2.12")}),-1.0]])]});
            var Q6;
            Q6=makeQuery(id+"F4.imprint","IMPRINT",FACE,{"disambiguationData":[TD([[makeQuery(id+"F4.imprint","IMPRINT",EDGE,{"derivedFrom":sQuery(id+"F4.wireOp",EDGE,"E40.1.3")}),-1.0]])]});
            var Q7;
            Q7=makeQuery(id+"F4.imprint","IMPRINT",FACE,{"disambiguationData":[TD([[makeQuery(id+"F4.imprint","IMPRINT",EDGE,{"derivedFrom":sQuery(id+"F4.wireOp",EDGE,"E40.1.10")}),-1.0]])]});
            var Q8;
            Q8=makeQuery(id+"F4.imprint","IMPRINT",FACE,{"disambiguationData":[TD([[makeQuery(id+"F4.imprint","IMPRINT",EDGE,{"derivedFrom":sQuery(id+"F4.wireOp",EDGE,"E40.1.12")}),-1.0]])]});
            var Q9;
            Q9=makeQuery(id+"F4.imprint","IMPRINT",FACE,{"disambiguationData":[TD([[makeQuery(id+"F4.imprint","IMPRINT",EDGE,{"derivedFrom":sQuery(id+"F4.wireOp",EDGE,"E23")}),-1.0]])]});
            var Q10;
            Q10=makeQuery(id+"F4.imprint","IMPRINT",FACE,{"disambiguationData":[TD([[makeQuery(id+"F4.imprint","IMPRINT",EDGE,{"derivedFrom":sQuery(id+"F4.wireOp",EDGE,"E25")}),-1.0]])]});
            var Q11;
            Q11=makeQuery(id+"F4.imprint","IMPRINT",FACE,{"disambiguationData":[TD([[makeQuery(id+"F4.imprint","IMPRINT",EDGE,{"derivedFrom":sQuery(id+"F4.wireOp",EDGE,"E16")}),1.0]])]});
            extrude(context, id + "F6", {"entities" : qUnion([Q0, Q1, Q2, Q3, Q4, Q5, Q6, Q7, Q8, Q9, Q10, Q11]), "operationType" : NewBodyOperationType.REMOVE, "oppositeDirection" : true, "depth" : 2.5 * mm});
        }
        {
            var Q0;
            Q0=makeQuery(id+"F5.boolean.opBoolean","COPY",EDGE,{"derivedFrom":makeQuery(id+"F5.opExtrude","SWEPT_EDGE",EDGE,{"disambiguationData":[OSD([sQuery(id+"F4.wireOp",EDGE,"E40.3.0"),sQuery(id+"F4.wireOp",EDGE,"E40.3.6")])]})});
            var Q1;
            Q1=makeQuery(id+"F5.boolean.opBoolean","COPY",EDGE,{"derivedFrom":makeQuery(id+"F5.opExtrude","SWEPT_EDGE",EDGE,{"disambiguationData":[OSD([sQuery(id+"F4.wireOp",EDGE,"E40.3.2"),sQuery(id+"F4.wireOp",EDGE,"E40.3.5")])]})});
            var Q2;
            Q2=makeQuery(id+"F6.boolean.opBoolean","COPY",EDGE,{"derivedFrom":makeQuery(id+"F6.opExtrude","SWEPT_EDGE",EDGE,{"disambiguationData":[OSD([sQuery(id+"F4.wireOp",EDGE,"E40.3.3"),sQuery(id+"F4.wireOp",EDGE,"E40.3.22")])]})});
            var Q3;
            Q3=makeQuery(id+"F6.boolean.opBoolean","COPY",EDGE,{"derivedFrom":makeQuery(id+"F6.opExtrude","SWEPT_EDGE",EDGE,{"disambiguationData":[OSD([sQuery(id+"F4.wireOp",EDGE,"E40.3.19"),sQuery(id+"F4.wireOp",EDGE,"E40.3.21")])]})});
            var Q4;
            Q4=makeQuery(id+"F5.boolean.opBoolean","COPY",EDGE,{"derivedFrom":makeQuery(id+"F5.opExtrude","SWEPT_EDGE",EDGE,{"disambiguationData":[OSD([sQuery(id+"F4.wireOp",EDGE,"E40.3.17"),sQuery(id+"F4.wireOp",EDGE,"E40.3.18")])]})});
            var Q5;
            Q5=makeQuery(id+"F6.boolean.opBoolean","COPY",EDGE,{"derivedFrom":makeQuery(id+"F6.opExtrude","SWEPT_EDGE",EDGE,{"disambiguationData":[OSD([sQuery(id+"F4.wireOp",EDGE,"E40.3.13"),sQuery(id+"F4.wireOp",EDGE,"E40.3.15")])]})});
            var Q6;
            Q6=makeQuery(id+"F5.boolean.opBoolean","COPY",EDGE,{"derivedFrom":makeQuery(id+"F5.opExtrude","SWEPT_EDGE",EDGE,{"disambiguationData":[OSD([sQuery(id+"F4.wireOp",EDGE,"E40.2.0"),sQuery(id+"F4.wireOp",EDGE,"E40.2.6")])]})});
            var Q7;
            Q7=makeQuery(id+"F5.boolean.opBoolean","COPY",EDGE,{"derivedFrom":makeQuery(id+"F5.opExtrude","SWEPT_EDGE",EDGE,{"disambiguationData":[OSD([sQuery(id+"F4.wireOp",EDGE,"E40.2.2"),sQuery(id+"F4.wireOp",EDGE,"E40.2.5")])]})});
            var Q8;
            Q8=makeQuery(id+"F6.boolean.opBoolean","COPY",EDGE,{"derivedFrom":makeQuery(id+"F6.opExtrude","SWEPT_EDGE",EDGE,{"disambiguationData":[OSD([sQuery(id+"F4.wireOp",EDGE,"E40.2.3"),sQuery(id+"F4.wireOp",EDGE,"E40.2.22")])]})});
            var Q9;
            Q9=makeQuery(id+"F6.boolean.opBoolean","COPY",EDGE,{"derivedFrom":makeQuery(id+"F6.opExtrude","SWEPT_EDGE",EDGE,{"disambiguationData":[OSD([sQuery(id+"F4.wireOp",EDGE,"E40.2.19"),sQuery(id+"F4.wireOp",EDGE,"E40.2.21")])]})});
            var Q10;
            Q10=makeQuery(id+"F5.boolean.opBoolean","COPY",EDGE,{"derivedFrom":makeQuery(id+"F5.opExtrude","SWEPT_EDGE",EDGE,{"disambiguationData":[OSD([sQuery(id+"F4.wireOp",EDGE,"E40.2.17"),sQuery(id+"F4.wireOp",EDGE,"E40.2.18")])]})});
            var Q11;
            Q11=makeQuery(id+"F6.boolean.opBoolean","COPY",EDGE,{"derivedFrom":makeQuery(id+"F6.opExtrude","SWEPT_EDGE",EDGE,{"disambiguationData":[OSD([sQuery(id+"F4.wireOp",EDGE,"E40.2.13"),sQuery(id+"F4.wireOp",EDGE,"E40.2.15")])]})});
            var Q12;
            Q12=makeQuery(id+"F5.boolean.opBoolean","COPY",EDGE,{"derivedFrom":makeQuery(id+"F5.opExtrude","SWEPT_EDGE",EDGE,{"disambiguationData":[OSD([sQuery(id+"F4.wireOp",EDGE,"E40.1.0"),sQuery(id+"F4.wireOp",EDGE,"E40.1.6")])]})});
            var Q13;
            Q13=makeQuery(id+"F5.boolean.opBoolean","COPY",EDGE,{"derivedFrom":makeQuery(id+"F5.opExtrude","SWEPT_EDGE",EDGE,{"disambiguationData":[OSD([sQuery(id+"F4.wireOp",EDGE,"E40.1.2"),sQuery(id+"F4.wireOp",EDGE,"E40.1.5")])]})});
            var Q14;
            Q14=makeQuery(id+"F6.boolean.opBoolean","COPY",EDGE,{"derivedFrom":makeQuery(id+"F6.opExtrude","SWEPT_EDGE",EDGE,{"disambiguationData":[OSD([sQuery(id+"F4.wireOp",EDGE,"E40.1.3"),sQuery(id+"F4.wireOp",EDGE,"E40.1.22")])]})});
            var Q15;
            Q15=makeQuery(id+"F6.boolean.opBoolean","COPY",EDGE,{"derivedFrom":makeQuery(id+"F6.opExtrude","SWEPT_EDGE",EDGE,{"disambiguationData":[OSD([sQuery(id+"F4.wireOp",EDGE,"E40.1.19"),sQuery(id+"F4.wireOp",EDGE,"E40.1.21")])]})});
            var Q16;
            Q16=makeQuery(id+"F5.boolean.opBoolean","COPY",EDGE,{"derivedFrom":makeQuery(id+"F5.opExtrude","SWEPT_EDGE",EDGE,{"disambiguationData":[OSD([sQuery(id+"F4.wireOp",EDGE,"E40.1.17"),sQuery(id+"F4.wireOp",EDGE,"E40.1.18")])]})});
            var Q17;
            Q17=makeQuery(id+"F6.boolean.opBoolean","COPY",EDGE,{"derivedFrom":makeQuery(id+"F6.opExtrude","SWEPT_EDGE",EDGE,{"disambiguationData":[OSD([sQuery(id+"F4.wireOp",EDGE,"E40.1.13"),sQuery(id+"F4.wireOp",EDGE,"E40.1.15")])]})});
            var Q18;
            Q18=makeQuery(id+"F5.boolean.opBoolean","COPY",EDGE,{"derivedFrom":makeQuery(id+"F5.opExtrude","SWEPT_EDGE",EDGE,{"disambiguationData":[OSD([sQuery(id+"F4.wireOp",EDGE,"E17"),sQuery(id+"F4.wireOp",EDGE,"E34.trimOffspring")])]})});
            var Q19;
            Q19=makeQuery(id+"F5.boolean.opBoolean","COPY",EDGE,{"derivedFrom":makeQuery(id+"F5.opExtrude","SWEPT_EDGE",EDGE,{"disambiguationData":[OSD([sQuery(id+"F4.wireOp",EDGE,"E21"),sQuery(id+"F4.wireOp",EDGE,"E33.trimOffspring")])]})});
            var Q20;
            Q20=makeQuery(id+"F6.boolean.opBoolean","COPY",EDGE,{"derivedFrom":makeQuery(id+"F6.opExtrude","SWEPT_EDGE",EDGE,{"disambiguationData":[OSD([sQuery(id+"F4.wireOp",EDGE,"E23"),sQuery(id+"F4.wireOp",EDGE,"E32.trimOffspring")])]})});
            var Q21;
            Q21=makeQuery(id+"F6.boolean.opBoolean","COPY",EDGE,{"derivedFrom":makeQuery(id+"F6.opExtrude","SWEPT_EDGE",EDGE,{"disambiguationData":[OSD([sQuery(id+"F4.wireOp",EDGE,"E25"),sQuery(id+"F4.wireOp",EDGE,"E31.trimOffspring")])]})});
            var Q22;
            Q22=makeQuery(id+"F5.boolean.opBoolean","COPY",EDGE,{"derivedFrom":makeQuery(id+"F5.opExtrude","SWEPT_EDGE",EDGE,{"disambiguationData":[OSD([sQuery(id+"F4.wireOp",EDGE,"E27"),sQuery(id+"F4.wireOp",EDGE,"E30.trimOffspring")])]})});
            var Q23;
            Q23=makeQuery(id+"F6.boolean.opBoolean","COPY",EDGE,{"derivedFrom":makeQuery(id+"F6.opExtrude","SWEPT_EDGE",EDGE,{"disambiguationData":[OSD([sQuery(id+"F4.wireOp",EDGE,"E19"),sQuery(id+"F4.wireOp",EDGE,"E29")])]})});
            var Q24;
            Q24=makeQuery(id+"F6.boolean.opBoolean","COPY",EDGE,{"derivedFrom":makeQuery(id+"F6.opExtrude","SWEPT_EDGE",EDGE,{"disambiguationData":[OSD([sQuery(id+"F4.wireOp",EDGE,"E16"),sQuery(id+"F4.wireOp",EDGE,"E19")])]})});
            var Q25;
            Q25=makeQuery(id+"F5.boolean.opBoolean","COPY",EDGE,{"derivedFrom":makeQuery(id+"F5.opExtrude","SWEPT_EDGE",EDGE,{"disambiguationData":[OSD([sQuery(id+"F4.wireOp",EDGE,"E28"),sQuery(id+"F4.wireOp",EDGE,"E30.trimOffspring")])]})});
            var Q26;
            Q26=makeQuery(id+"F6.boolean.opBoolean","COPY",EDGE,{"derivedFrom":makeQuery(id+"F6.opExtrude","SWEPT_EDGE",EDGE,{"disambiguationData":[OSD([sQuery(id+"F4.wireOp",EDGE,"E26"),sQuery(id+"F4.wireOp",EDGE,"E31.trimOffspring")])]})});
            var Q27;
            Q27=makeQuery(id+"F6.boolean.opBoolean","COPY",EDGE,{"derivedFrom":makeQuery(id+"F6.opExtrude","SWEPT_EDGE",EDGE,{"disambiguationData":[OSD([sQuery(id+"F4.wireOp",EDGE,"E24"),sQuery(id+"F4.wireOp",EDGE,"E32.trimOffspring")])]})});
            var Q28;
            Q28=makeQuery(id+"F5.boolean.opBoolean","COPY",EDGE,{"derivedFrom":makeQuery(id+"F5.opExtrude","SWEPT_EDGE",EDGE,{"disambiguationData":[OSD([sQuery(id+"F4.wireOp",EDGE,"E20"),sQuery(id+"F4.wireOp",EDGE,"E34.trimOffspring")])]})});
            var Q29;
            Q29=makeQuery(id+"F5.boolean.opBoolean","COPY",EDGE,{"derivedFrom":makeQuery(id+"F5.opExtrude","SWEPT_EDGE",EDGE,{"disambiguationData":[OSD([sQuery(id+"F4.wireOp",EDGE,"E22"),sQuery(id+"F4.wireOp",EDGE,"E33.trimOffspring")])]})});
            var Q30;
            Q30=makeQuery(id+"F6.boolean.opBoolean","COPY",EDGE,{"derivedFrom":makeQuery(id+"F6.opExtrude","SWEPT_EDGE",EDGE,{"disambiguationData":[OSD([sQuery(id+"F4.wireOp",EDGE,"E40.1.13"),sQuery(id+"F4.wireOp",EDGE,"E40.1.14")])]})});
            var Q31;
            Q31=makeQuery(id+"F5.boolean.opBoolean","COPY",EDGE,{"derivedFrom":makeQuery(id+"F5.opExtrude","SWEPT_EDGE",EDGE,{"disambiguationData":[OSD([sQuery(id+"F4.wireOp",EDGE,"E40.1.16"),sQuery(id+"F4.wireOp",EDGE,"E40.1.17")])]})});
            var Q32;
            Q32=makeQuery(id+"F6.boolean.opBoolean","COPY",EDGE,{"derivedFrom":makeQuery(id+"F6.opExtrude","SWEPT_EDGE",EDGE,{"disambiguationData":[OSD([sQuery(id+"F4.wireOp",EDGE,"E40.1.19"),sQuery(id+"F4.wireOp",EDGE,"E40.1.20")])]})});
            var Q33;
            Q33=makeQuery(id+"F5.boolean.opBoolean","COPY",EDGE,{"derivedFrom":makeQuery(id+"F5.opExtrude","SWEPT_EDGE",EDGE,{"disambiguationData":[OSD([sQuery(id+"F4.wireOp",EDGE,"E40.1.1"),sQuery(id+"F4.wireOp",EDGE,"E40.1.6")])]})});
            var Q34;
            Q34=makeQuery(id+"F5.boolean.opBoolean","COPY",EDGE,{"derivedFrom":makeQuery(id+"F5.opExtrude","SWEPT_EDGE",EDGE,{"disambiguationData":[OSD([sQuery(id+"F4.wireOp",EDGE,"E40.1.4"),sQuery(id+"F4.wireOp",EDGE,"E40.1.5")])]})});
            var Q35;
            Q35=makeQuery(id+"F6.boolean.opBoolean","COPY",EDGE,{"derivedFrom":makeQuery(id+"F6.opExtrude","SWEPT_EDGE",EDGE,{"disambiguationData":[OSD([sQuery(id+"F4.wireOp",EDGE,"E40.2.13"),sQuery(id+"F4.wireOp",EDGE,"E40.2.14")])]})});
            var Q36;
            Q36=makeQuery(id+"F5.boolean.opBoolean","COPY",EDGE,{"derivedFrom":makeQuery(id+"F5.opExtrude","SWEPT_EDGE",EDGE,{"disambiguationData":[OSD([sQuery(id+"F4.wireOp",EDGE,"E40.2.16"),sQuery(id+"F4.wireOp",EDGE,"E40.2.17")])]})});
            var Q37;
            Q37=makeQuery(id+"F5.boolean.opBoolean","COPY",EDGE,{"derivedFrom":makeQuery(id+"F5.opExtrude","SWEPT_EDGE",EDGE,{"disambiguationData":[OSD([sQuery(id+"F4.wireOp",EDGE,"E40.2.1"),sQuery(id+"F4.wireOp",EDGE,"E40.2.6")])]})});
            var Q38;
            Q38=makeQuery(id+"F5.boolean.opBoolean","COPY",EDGE,{"derivedFrom":makeQuery(id+"F5.opExtrude","SWEPT_EDGE",EDGE,{"disambiguationData":[OSD([sQuery(id+"F4.wireOp",EDGE,"E40.2.4"),sQuery(id+"F4.wireOp",EDGE,"E40.2.5")])]})});
            var Q39;
            Q39=makeQuery(id+"F6.boolean.opBoolean","COPY",EDGE,{"derivedFrom":makeQuery(id+"F6.opExtrude","SWEPT_EDGE",EDGE,{"disambiguationData":[OSD([sQuery(id+"F4.wireOp",EDGE,"E40.2.19"),sQuery(id+"F4.wireOp",EDGE,"E40.2.20")])]})});
            var Q40;
            Q40=makeQuery(id+"F6.boolean.opBoolean","COPY",EDGE,{"derivedFrom":makeQuery(id+"F6.opExtrude","SWEPT_EDGE",EDGE,{"disambiguationData":[OSD([sQuery(id+"F4.wireOp",EDGE,"E40.2.22"),sQuery(id+"F4.wireOp",EDGE,"E40.2.23")])]})});
            var Q41;
            Q41=makeQuery(id+"F6.boolean.opBoolean","COPY",EDGE,{"derivedFrom":makeQuery(id+"F6.opExtrude","SWEPT_EDGE",EDGE,{"disambiguationData":[OSD([sQuery(id+"F4.wireOp",EDGE,"E40.3.13"),sQuery(id+"F4.wireOp",EDGE,"E40.3.14")])]})});
            var Q42;
            Q42=makeQuery(id+"F5.boolean.opBoolean","COPY",EDGE,{"derivedFrom":makeQuery(id+"F5.opExtrude","SWEPT_EDGE",EDGE,{"disambiguationData":[OSD([sQuery(id+"F4.wireOp",EDGE,"E40.3.16"),sQuery(id+"F4.wireOp",EDGE,"E40.3.17")])]})});
            var Q43;
            Q43=makeQuery(id+"F6.boolean.opBoolean","COPY",EDGE,{"derivedFrom":makeQuery(id+"F6.opExtrude","SWEPT_EDGE",EDGE,{"disambiguationData":[OSD([sQuery(id+"F4.wireOp",EDGE,"E40.3.19"),sQuery(id+"F4.wireOp",EDGE,"E40.3.20")])]})});
            var Q44;
            Q44=makeQuery(id+"F6.boolean.opBoolean","COPY",EDGE,{"derivedFrom":makeQuery(id+"F6.opExtrude","SWEPT_EDGE",EDGE,{"disambiguationData":[OSD([sQuery(id+"F4.wireOp",EDGE,"E40.3.22"),sQuery(id+"F4.wireOp",EDGE,"E40.3.23")])]})});
            var Q45;
            Q45=makeQuery(id+"F5.boolean.opBoolean","COPY",EDGE,{"derivedFrom":makeQuery(id+"F5.opExtrude","SWEPT_EDGE",EDGE,{"disambiguationData":[OSD([sQuery(id+"F4.wireOp",EDGE,"E40.3.4"),sQuery(id+"F4.wireOp",EDGE,"E40.3.5")])]})});
            var Q46;
            Q46=makeQuery(id+"F5.boolean.opBoolean","COPY",EDGE,{"derivedFrom":makeQuery(id+"F5.opExtrude","SWEPT_EDGE",EDGE,{"disambiguationData":[OSD([sQuery(id+"F4.wireOp",EDGE,"E40.3.1"),sQuery(id+"F4.wireOp",EDGE,"E40.3.6")])]})});
            var Q47;
            Q47=makeQuery(id+"F5.boolean.opBoolean","COPY",EDGE,{"derivedFrom":makeQuery(id+"F5.opExtrude","SWEPT_EDGE",EDGE,{"disambiguationData":[OSD([sQuery(id+"F4.wireOp",EDGE,"E40.3.0"),sQuery(id+"F4.wireOp",EDGE,"E40.3.7")])]})});
            var Q48;
            Q48=makeQuery(id+"F5.boolean.opBoolean","COPY",EDGE,{"derivedFrom":makeQuery(id+"F5.opExtrude","SWEPT_EDGE",EDGE,{"disambiguationData":[OSD([sQuery(id+"F4.wireOp",EDGE,"E40.3.2"),sQuery(id+"F4.wireOp",EDGE,"E40.3.8")])]})});
            var Q49;
            Q49=makeQuery(id+"F6.boolean.opBoolean","COPY",EDGE,{"derivedFrom":makeQuery(id+"F6.opExtrude","SWEPT_EDGE",EDGE,{"disambiguationData":[OSD([sQuery(id+"F4.wireOp",EDGE,"E40.3.3"),sQuery(id+"F4.wireOp",EDGE,"E40.3.9")])]})});
            var Q50;
            Q50=makeQuery(id+"F6.boolean.opBoolean","COPY",EDGE,{"derivedFrom":makeQuery(id+"F6.opExtrude","SWEPT_EDGE",EDGE,{"disambiguationData":[OSD([sQuery(id+"F4.wireOp",EDGE,"E40.3.10"),sQuery(id+"F4.wireOp",EDGE,"E40.3.21")])]})});
            var Q51;
            Q51=makeQuery(id+"F6.boolean.opBoolean","COPY",EDGE,{"derivedFrom":makeQuery(id+"F6.opExtrude","SWEPT_EDGE",EDGE,{"disambiguationData":[OSD([sQuery(id+"F4.wireOp",EDGE,"E40.3.12"),sQuery(id+"F4.wireOp",EDGE,"E40.3.15")])]})});
            var Q52;
            Q52=makeQuery(id+"F5.boolean.opBoolean","COPY",EDGE,{"derivedFrom":makeQuery(id+"F5.opExtrude","SWEPT_EDGE",EDGE,{"disambiguationData":[OSD([sQuery(id+"F4.wireOp",EDGE,"E40.3.11"),sQuery(id+"F4.wireOp",EDGE,"E40.3.18")])]})});
            var Q53;
            Q53=makeQuery(id+"F5.boolean.opBoolean","COPY",EDGE,{"derivedFrom":makeQuery(id+"F5.opExtrude","SWEPT_EDGE",EDGE,{"disambiguationData":[OSD([sQuery(id+"F4.wireOp",EDGE,"E40.2.0"),sQuery(id+"F4.wireOp",EDGE,"E40.2.7")])]})});
            var Q54;
            Q54=makeQuery(id+"F5.boolean.opBoolean","COPY",EDGE,{"derivedFrom":makeQuery(id+"F5.opExtrude","SWEPT_EDGE",EDGE,{"disambiguationData":[OSD([sQuery(id+"F4.wireOp",EDGE,"E40.2.2"),sQuery(id+"F4.wireOp",EDGE,"E40.2.8")])]})});
            var Q55;
            Q55=makeQuery(id+"F6.boolean.opBoolean","COPY",EDGE,{"derivedFrom":makeQuery(id+"F6.opExtrude","SWEPT_EDGE",EDGE,{"disambiguationData":[OSD([sQuery(id+"F4.wireOp",EDGE,"E40.2.3"),sQuery(id+"F4.wireOp",EDGE,"E40.2.9")])]})});
            var Q56;
            Q56=makeQuery(id+"F6.boolean.opBoolean","COPY",EDGE,{"derivedFrom":makeQuery(id+"F6.opExtrude","SWEPT_EDGE",EDGE,{"disambiguationData":[OSD([sQuery(id+"F4.wireOp",EDGE,"E40.2.10"),sQuery(id+"F4.wireOp",EDGE,"E40.2.21")])]})});
            var Q57;
            Q57=makeQuery(id+"F5.boolean.opBoolean","COPY",EDGE,{"derivedFrom":makeQuery(id+"F5.opExtrude","SWEPT_EDGE",EDGE,{"disambiguationData":[OSD([sQuery(id+"F4.wireOp",EDGE,"E40.2.11"),sQuery(id+"F4.wireOp",EDGE,"E40.2.18")])]})});
            var Q58;
            Q58=makeQuery(id+"F6.boolean.opBoolean","COPY",EDGE,{"derivedFrom":makeQuery(id+"F6.opExtrude","SWEPT_EDGE",EDGE,{"disambiguationData":[OSD([sQuery(id+"F4.wireOp",EDGE,"E40.2.12"),sQuery(id+"F4.wireOp",EDGE,"E40.2.15")])]})});
            var Q59;
            Q59=makeQuery(id+"F5.boolean.opBoolean","COPY",EDGE,{"derivedFrom":makeQuery(id+"F5.opExtrude","SWEPT_EDGE",EDGE,{"disambiguationData":[OSD([sQuery(id+"F4.wireOp",EDGE,"E40.1.0"),sQuery(id+"F4.wireOp",EDGE,"E40.1.7")])]})});
            var Q60;
            Q60=makeQuery(id+"F5.boolean.opBoolean","COPY",EDGE,{"derivedFrom":makeQuery(id+"F5.opExtrude","SWEPT_EDGE",EDGE,{"disambiguationData":[OSD([sQuery(id+"F4.wireOp",EDGE,"E40.1.2"),sQuery(id+"F4.wireOp",EDGE,"E40.1.8")])]})});
            var Q61;
            Q61=makeQuery(id+"F6.boolean.opBoolean","COPY",EDGE,{"derivedFrom":makeQuery(id+"F6.opExtrude","SWEPT_EDGE",EDGE,{"disambiguationData":[OSD([sQuery(id+"F4.wireOp",EDGE,"E40.1.3"),sQuery(id+"F4.wireOp",EDGE,"E40.1.9")])]})});
            var Q62;
            Q62=makeQuery(id+"F6.boolean.opBoolean","COPY",EDGE,{"derivedFrom":makeQuery(id+"F6.opExtrude","SWEPT_EDGE",EDGE,{"disambiguationData":[OSD([sQuery(id+"F4.wireOp",EDGE,"E40.1.10"),sQuery(id+"F4.wireOp",EDGE,"E40.1.21")])]})});
            var Q63;
            Q63=makeQuery(id+"F6.boolean.opBoolean","COPY",EDGE,{"derivedFrom":makeQuery(id+"F6.opExtrude","SWEPT_EDGE",EDGE,{"disambiguationData":[OSD([sQuery(id+"F4.wireOp",EDGE,"E40.1.12"),sQuery(id+"F4.wireOp",EDGE,"E40.1.15")])]})});
            var Q64;
            Q64=makeQuery(id+"F5.boolean.opBoolean","COPY",EDGE,{"derivedFrom":makeQuery(id+"F5.opExtrude","SWEPT_EDGE",EDGE,{"disambiguationData":[OSD([sQuery(id+"F4.wireOp",EDGE,"E40.1.11"),sQuery(id+"F4.wireOp",EDGE,"E40.1.18")])]})});
            var Q65;
            Q65=makeQuery(id+"F5.boolean.opBoolean","COPY",EDGE,{"derivedFrom":makeQuery(id+"F5.opExtrude","SWEPT_EDGE",EDGE,{"disambiguationData":[OSD([sQuery(id+"F4.wireOp",EDGE,"E17"),sQuery(id+"F4.wireOp",EDGE,"E35.trimOffspring")])]})});
            var Q66;
            Q66=makeQuery(id+"F5.boolean.opBoolean","COPY",EDGE,{"derivedFrom":makeQuery(id+"F5.opExtrude","SWEPT_EDGE",EDGE,{"disambiguationData":[OSD([sQuery(id+"F4.wireOp",EDGE,"E21"),sQuery(id+"F4.wireOp",EDGE,"E36.trimOffspring")])]})});
            var Q67;
            Q67=makeQuery(id+"F6.boolean.opBoolean","COPY",EDGE,{"derivedFrom":makeQuery(id+"F6.opExtrude","SWEPT_EDGE",EDGE,{"disambiguationData":[OSD([sQuery(id+"F4.wireOp",EDGE,"E23"),sQuery(id+"F4.wireOp",EDGE,"E37.trimOffspring")])]})});
            var Q68;
            Q68=makeQuery(id+"F6.boolean.opBoolean","COPY",EDGE,{"derivedFrom":makeQuery(id+"F6.opExtrude","SWEPT_EDGE",EDGE,{"disambiguationData":[OSD([sQuery(id+"F4.wireOp",EDGE,"E25"),sQuery(id+"F4.wireOp",EDGE,"E38.trimOffspring")])]})});
            var Q69;
            Q69=makeQuery(id+"F5.boolean.opBoolean","COPY",EDGE,{"derivedFrom":makeQuery(id+"F5.opExtrude","SWEPT_EDGE",EDGE,{"disambiguationData":[OSD([sQuery(id+"F4.wireOp",EDGE,"E27"),sQuery(id+"F4.wireOp",EDGE,"E39.trimOffspring")])]})});
            var Q70;
            Q70=makeQuery(id+"F6.boolean.opBoolean","COPY",EDGE,{"derivedFrom":makeQuery(id+"F6.opExtrude","SWEPT_EDGE",EDGE,{"disambiguationData":[OSD([sQuery(id+"F4.wireOp",EDGE,"E18"),sQuery(id+"F4.wireOp",EDGE,"E29")])]})});
            var Q71;
            Q71=makeQuery(id+"F5.boolean.opBoolean","COPY",EDGE,{"derivedFrom":makeQuery(id+"F5.opExtrude","SWEPT_EDGE",EDGE,{"disambiguationData":[OSD([sQuery(id+"F4.wireOp",EDGE,"E40.3.1"),sQuery(id+"F4.wireOp",EDGE,"E40.3.7")])]})});
            var Q72;
            Q72=makeQuery(id+"F5.boolean.opBoolean","COPY",EDGE,{"derivedFrom":makeQuery(id+"F5.opExtrude","SWEPT_EDGE",EDGE,{"disambiguationData":[OSD([sQuery(id+"F4.wireOp",EDGE,"E40.3.4"),sQuery(id+"F4.wireOp",EDGE,"E40.3.8")])]})});
            var Q73;
            Q73=makeQuery(id+"F6.boolean.opBoolean","COPY",EDGE,{"derivedFrom":makeQuery(id+"F6.opExtrude","SWEPT_EDGE",EDGE,{"disambiguationData":[OSD([sQuery(id+"F4.wireOp",EDGE,"E40.3.9"),sQuery(id+"F4.wireOp",EDGE,"E40.3.23")])]})});
            var Q74;
            Q74=makeQuery(id+"F6.boolean.opBoolean","COPY",EDGE,{"derivedFrom":makeQuery(id+"F6.opExtrude","SWEPT_EDGE",EDGE,{"disambiguationData":[OSD([sQuery(id+"F4.wireOp",EDGE,"E40.3.10"),sQuery(id+"F4.wireOp",EDGE,"E40.3.20")])]})});
            var Q75;
            Q75=makeQuery(id+"F5.boolean.opBoolean","COPY",EDGE,{"derivedFrom":makeQuery(id+"F5.opExtrude","SWEPT_EDGE",EDGE,{"disambiguationData":[OSD([sQuery(id+"F4.wireOp",EDGE,"E40.3.11"),sQuery(id+"F4.wireOp",EDGE,"E40.3.16")])]})});
            var Q76;
            Q76=makeQuery(id+"F6.boolean.opBoolean","COPY",EDGE,{"derivedFrom":makeQuery(id+"F6.opExtrude","SWEPT_EDGE",EDGE,{"disambiguationData":[OSD([sQuery(id+"F4.wireOp",EDGE,"E40.3.12"),sQuery(id+"F4.wireOp",EDGE,"E40.3.14")])]})});
            var Q77;
            Q77=makeQuery(id+"F5.boolean.opBoolean","COPY",EDGE,{"derivedFrom":makeQuery(id+"F5.opExtrude","SWEPT_EDGE",EDGE,{"disambiguationData":[OSD([sQuery(id+"F4.wireOp",EDGE,"E40.2.1"),sQuery(id+"F4.wireOp",EDGE,"E40.2.7")])]})});
            var Q78;
            Q78=makeQuery(id+"F5.boolean.opBoolean","COPY",EDGE,{"derivedFrom":makeQuery(id+"F5.opExtrude","SWEPT_EDGE",EDGE,{"disambiguationData":[OSD([sQuery(id+"F4.wireOp",EDGE,"E40.2.4"),sQuery(id+"F4.wireOp",EDGE,"E40.2.8")])]})});
            var Q79;
            Q79=makeQuery(id+"F6.boolean.opBoolean","COPY",EDGE,{"derivedFrom":makeQuery(id+"F6.opExtrude","SWEPT_EDGE",EDGE,{"disambiguationData":[OSD([sQuery(id+"F4.wireOp",EDGE,"E40.2.9"),sQuery(id+"F4.wireOp",EDGE,"E40.2.23")])]})});
            var Q80;
            Q80=makeQuery(id+"F6.boolean.opBoolean","COPY",EDGE,{"derivedFrom":makeQuery(id+"F6.opExtrude","SWEPT_EDGE",EDGE,{"disambiguationData":[OSD([sQuery(id+"F4.wireOp",EDGE,"E40.2.10"),sQuery(id+"F4.wireOp",EDGE,"E40.2.20")])]})});
            var Q81;
            Q81=makeQuery(id+"F5.boolean.opBoolean","COPY",EDGE,{"derivedFrom":makeQuery(id+"F5.opExtrude","SWEPT_EDGE",EDGE,{"disambiguationData":[OSD([sQuery(id+"F4.wireOp",EDGE,"E40.2.11"),sQuery(id+"F4.wireOp",EDGE,"E40.2.16")])]})});
            var Q82;
            Q82=makeQuery(id+"F6.boolean.opBoolean","COPY",EDGE,{"derivedFrom":makeQuery(id+"F6.opExtrude","SWEPT_EDGE",EDGE,{"disambiguationData":[OSD([sQuery(id+"F4.wireOp",EDGE,"E40.2.12"),sQuery(id+"F4.wireOp",EDGE,"E40.2.14")])]})});
            var Q83;
            Q83=makeQuery(id+"F5.boolean.opBoolean","COPY",EDGE,{"derivedFrom":makeQuery(id+"F5.opExtrude","SWEPT_EDGE",EDGE,{"disambiguationData":[OSD([sQuery(id+"F4.wireOp",EDGE,"E40.1.1"),sQuery(id+"F4.wireOp",EDGE,"E40.1.7")])]})});
            var Q84;
            Q84=makeQuery(id+"F5.boolean.opBoolean","COPY",EDGE,{"derivedFrom":makeQuery(id+"F5.opExtrude","SWEPT_EDGE",EDGE,{"disambiguationData":[OSD([sQuery(id+"F4.wireOp",EDGE,"E40.1.4"),sQuery(id+"F4.wireOp",EDGE,"E40.1.8")])]})});
            var Q85;
            Q85=makeQuery(id+"F6.boolean.opBoolean","COPY",EDGE,{"derivedFrom":makeQuery(id+"F6.opExtrude","SWEPT_EDGE",EDGE,{"disambiguationData":[OSD([sQuery(id+"F4.wireOp",EDGE,"E40.1.9"),sQuery(id+"F4.wireOp",EDGE,"E40.1.23")])]})});
            var Q86;
            Q86=makeQuery(id+"F6.boolean.opBoolean","COPY",EDGE,{"derivedFrom":makeQuery(id+"F6.opExtrude","SWEPT_EDGE",EDGE,{"disambiguationData":[OSD([sQuery(id+"F4.wireOp",EDGE,"E40.1.10"),sQuery(id+"F4.wireOp",EDGE,"E40.1.20")])]})});
            var Q87;
            Q87=makeQuery(id+"F5.boolean.opBoolean","COPY",EDGE,{"derivedFrom":makeQuery(id+"F5.opExtrude","SWEPT_EDGE",EDGE,{"disambiguationData":[OSD([sQuery(id+"F4.wireOp",EDGE,"E40.1.11"),sQuery(id+"F4.wireOp",EDGE,"E40.1.16")])]})});
            var Q88;
            Q88=makeQuery(id+"F6.boolean.opBoolean","COPY",EDGE,{"derivedFrom":makeQuery(id+"F6.opExtrude","SWEPT_EDGE",EDGE,{"disambiguationData":[OSD([sQuery(id+"F4.wireOp",EDGE,"E40.1.12"),sQuery(id+"F4.wireOp",EDGE,"E40.1.14")])]})});
            var Q89;
            Q89=makeQuery(id+"F5.boolean.opBoolean","COPY",EDGE,{"derivedFrom":makeQuery(id+"F5.opExtrude","SWEPT_EDGE",EDGE,{"disambiguationData":[OSD([sQuery(id+"F4.wireOp",EDGE,"E20"),sQuery(id+"F4.wireOp",EDGE,"E35.trimOffspring")])]})});
            var Q90;
            Q90=makeQuery(id+"F5.boolean.opBoolean","COPY",EDGE,{"derivedFrom":makeQuery(id+"F5.opExtrude","SWEPT_EDGE",EDGE,{"disambiguationData":[OSD([sQuery(id+"F4.wireOp",EDGE,"E22"),sQuery(id+"F4.wireOp",EDGE,"E36.trimOffspring")])]})});
            var Q91;
            Q91=makeQuery(id+"F6.boolean.opBoolean","COPY",EDGE,{"derivedFrom":makeQuery(id+"F6.opExtrude","SWEPT_EDGE",EDGE,{"disambiguationData":[OSD([sQuery(id+"F4.wireOp",EDGE,"E24"),sQuery(id+"F4.wireOp",EDGE,"E37.trimOffspring")])]})});
            var Q92;
            Q92=makeQuery(id+"F6.boolean.opBoolean","COPY",EDGE,{"derivedFrom":makeQuery(id+"F6.opExtrude","SWEPT_EDGE",EDGE,{"disambiguationData":[OSD([sQuery(id+"F4.wireOp",EDGE,"E26"),sQuery(id+"F4.wireOp",EDGE,"E38.trimOffspring")])]})});
            var Q93;
            Q93=makeQuery(id+"F5.boolean.opBoolean","COPY",EDGE,{"derivedFrom":makeQuery(id+"F5.opExtrude","SWEPT_EDGE",EDGE,{"disambiguationData":[OSD([sQuery(id+"F4.wireOp",EDGE,"E28"),sQuery(id+"F4.wireOp",EDGE,"E39.trimOffspring")])]})});
            var Q94;
            Q94=makeQuery(id+"F6.boolean.opBoolean","COPY",EDGE,{"derivedFrom":makeQuery(id+"F6.opExtrude","SWEPT_EDGE",EDGE,{"disambiguationData":[OSD([sQuery(id+"F4.wireOp",EDGE,"E16"),sQuery(id+"F4.wireOp",EDGE,"E18")])]})});
            var Q95;
            Q95=makeQuery(id+"F6.boolean.opBoolean","COPY",EDGE,{"derivedFrom":makeQuery(id+"F6.opExtrude","SWEPT_EDGE",EDGE,{"disambiguationData":[OSD([sQuery(id+"F4.wireOp",EDGE,"E40.1.22"),sQuery(id+"F4.wireOp",EDGE,"E40.1.23")])]})});
            fillet(context, id + "F7", {"entities" : qUnion([Q0, Q1, Q2, Q3, Q4, Q5, Q6, Q7, Q8, Q9, Q10, Q11, Q12, Q13, Q14, Q15, Q16, Q17, Q18, Q19, Q20, Q21, Q22, Q23, Q24, Q25, Q26, Q27, Q28, Q29, Q30, Q31, Q32, Q33, Q34, Q35, Q36, Q37, Q38, Q39, Q40, Q41, Q42, Q43, Q44, Q45, Q46, Q47, Q48, Q49, Q50, Q51, Q52, Q53, Q54, Q55, Q56, Q57, Q58, Q59, Q60, Q61, Q62, Q63, Q64, Q65, Q66, Q67, Q68, Q69, Q70, Q71, Q72, Q73, Q74, Q75, Q76, Q77, Q78, Q79, Q80, Q81, Q82, Q83, Q84, Q85, Q86, Q87, Q88, Q89, Q90, Q91, Q92, Q93, Q94, Q95]), "radius" : 2 * mm, "tangentPropagation" : true, "allowEdgeOverflow" : false});
        }
    });
